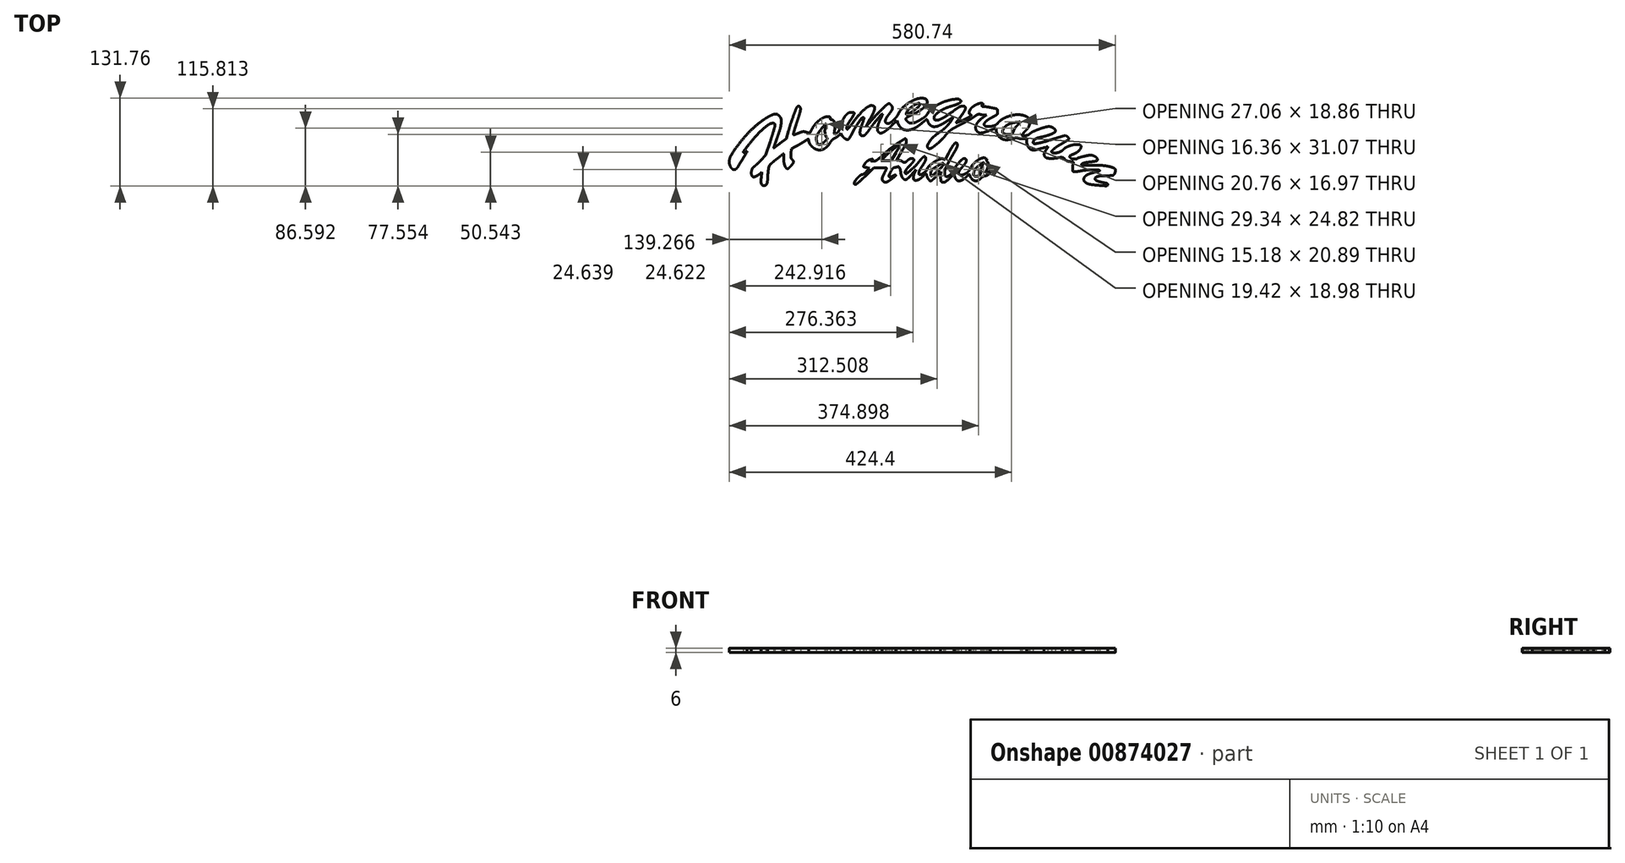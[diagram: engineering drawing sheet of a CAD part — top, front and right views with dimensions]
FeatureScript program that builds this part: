
annotation { "Feature Type Name" : "Feature", "Feature Type Description" : "" }
export const myFeature = defineFeature(function(context is Context, id is Id, definition is map)
    precondition{}
    {
        {
            var Q0;
            Q0=qCreatedBy(makeId("Top.planeOp"),FACE);
            var sketch = newSketch(context, id + "F0", { "sketchPlane" : qUnion([Q0])});
            skArc(sketch, "E0", {"start": v(-9.14, 64.5) * mm, "mid": v(-13.46, 62.75) * mm, "end": v(-17.6, 60.6) * mm});
            skArc(sketch, "E1", {"start": v(-17.6, 60.6) * mm, "mid": v(-21.63, 58.07) * mm, "end": v(-25.43, 55.2) * mm});
            skArc(sketch, "E2", {"start": v(-25.43, 55.2) * mm, "mid": v(-28.76, 52.2) * mm, "end": v(-31.81, 48.92) * mm});
            skArc(sketch, "E3", {"start": v(-31.81, 48.92) * mm, "mid": v(-34.1, 45.82) * mm, "end": v(-35.94, 42.44) * mm});
            skArc(sketch, "E4", {"start": v(-35.94, 42.44) * mm, "mid": v(-36.95, 40.52) * mm, "end": v(-38.16, 38.74) * mm});
            skArc(sketch, "E5", {"start": v(-38.16, 38.74) * mm, "mid": v(-39.88, 36.6) * mm, "end": v(-41.73, 34.56) * mm});
            skArc(sketch, "E6", {"start": v(-41.73, 34.56) * mm, "mid": v(-43.68, 32.62) * mm, "end": v(-45.74, 30.8) * mm});
            skArc(sketch, "E7", {"start": v(-45.74, 30.8) * mm, "mid": v(-47.5, 29.48) * mm, "end": v(-49.38, 28.36) * mm});
            skArc(sketch, "E8", {"start": v(-49.38, 28.36) * mm, "mid": v(-50.4, 27.96) * mm, "end": v(-51.5, 27.79) * mm});
            skArc(sketch, "E9", {"start": v(-51.5, 27.79) * mm, "mid": v(-52.56, 27.87) * mm, "end": v(-53.58, 28.21) * mm});
            skArc(sketch, "E10", {"start": v(-53.58, 28.21) * mm, "mid": v(-54.41, 28.76) * mm, "end": v(-55.07, 29.51) * mm});
            skArc(sketch, "E11", {"start": v(-55.07, 29.51) * mm, "mid": v(-55.48, 30.4) * mm, "end": v(-55.63, 31.35) * mm});
            skArc(sketch, "E12", {"start": v(-55.63, 31.35) * mm, "mid": v(-55.54, 32.43) * mm, "end": v(-55.28, 33.49) * mm});
            skArc(sketch, "E13", {"start": v(-55.28, 33.49) * mm, "mid": v(-54.82, 34.7) * mm, "end": v(-54.25, 35.85) * mm});
            skArc(sketch, "E14", {"start": v(-54.25, 35.85) * mm, "mid": v(-53.33, 37.4) * mm, "end": v(-52.32, 38.88) * mm});
            skArc(sketch, "E15", {"start": v(-52.32, 38.88) * mm, "mid": v(-50.67, 41.1) * mm, "end": v(-48.97, 43.31) * mm});
            skArc(sketch, "E16", {"start": v(-48.97, 43.31) * mm, "mid": v(-47.41, 45.42) * mm, "end": v(-45.95, 47.6) * mm});
            skArc(sketch, "E17", {"start": v(-45.95, 47.6) * mm, "mid": v(-45.26, 48.98) * mm, "end": v(-44.87, 50.47) * mm});
            skArc(sketch, "E18", {"start": v(-44.87, 50.47) * mm, "mid": v(-44.87, 51.74) * mm, "end": v(-45.26, 52.95) * mm});
            skArc(sketch, "E19", {"start": v(-45.26, 52.95) * mm, "mid": v(-46.09, 54.36) * mm, "end": v(-47.12, 55.65) * mm});
            skArc(sketch, "E20", {"start": v(-47.12, 55.65) * mm, "mid": v(-47.8, 56.35) * mm, "end": v(-48.5, 57.01) * mm});
            skArc(sketch, "E21", {"start": v(-48.5, 57.01) * mm, "mid": v(-48.98, 57.36) * mm, "end": v(-49.5, 57.61) * mm});
            skArc(sketch, "E22", {"start": v(-49.5, 57.61) * mm, "mid": v(-49.98, 57.71) * mm, "end": v(-50.45, 57.68) * mm});
            skArc(sketch, "E23", {"start": v(-50.45, 57.68) * mm, "mid": v(-51.03, 57.52) * mm, "end": v(-51.58, 57.28) * mm});
            skArc(sketch, "E24", {"start": v(-51.58, 57.28) * mm, "mid": v(-53.01, 56.38) * mm, "end": v(-54.32, 55.31) * mm});
            skArc(sketch, "E25", {"start": v(-54.32, 55.31) * mm, "mid": v(-57.3, 52.5) * mm, "end": v(-60.23, 49.63) * mm});
            skArc(sketch, "E26", {"start": v(-60.23, 49.63) * mm, "mid": v(-63.84, 46.03) * mm, "end": v(-67.38, 42.37) * mm});
            skArc(sketch, "E27", {"start": v(-67.38, 42.37) * mm, "mid": v(-71.44, 38.08) * mm, "end": v(-75.46, 33.75) * mm});
            skLineSegment(sketch, "E28", {"start": v(-75.46, 33.75) * mm, "end": v(-84.65, 23.75) * mm});
            skLineSegment(sketch, "E29", {"start": v(-84.65, 23.75) * mm, "end": v(-78.56, 34.4) * mm});
            skArc(sketch, "E30", {"start": v(-78.56, 34.4) * mm, "mid": v(-77.3, 36.66) * mm, "end": v(-76.1, 38.93) * mm});
            skArc(sketch, "E31", {"start": v(-76.1, 38.93) * mm, "mid": v(-75.03, 41.05) * mm, "end": v(-74.03, 43.2) * mm});
            skArc(sketch, "E32", {"start": v(-74.03, 43.2) * mm, "mid": v(-73.24, 45.02) * mm, "end": v(-72.5, 46.85) * mm});
            skArc(sketch, "E33", {"start": v(-72.5, 46.85) * mm, "mid": v(-72.14, 47.97) * mm, "end": v(-71.92, 49.12) * mm});
            skArc(sketch, "E34", {"start": v(-71.92, 49.12) * mm, "mid": v(-71.78, 50.3) * mm, "end": v(-71.69, 51.49) * mm});
            skArc(sketch, "E35", {"start": v(-71.69, 51.49) * mm, "mid": v(-71.72, 52.11) * mm, "end": v(-71.89, 52.71) * mm});
            skArc(sketch, "E36", {"start": v(-71.89, 52.71) * mm, "mid": v(-72.16, 53.18) * mm, "end": v(-72.55, 53.56) * mm});
            skArc(sketch, "E37", {"start": v(-72.55, 53.56) * mm, "mid": v(-73.25, 54) * mm, "end": v(-73.99, 54.37) * mm});
            skArc(sketch, "E38", {"start": v(-73.99, 54.37) * mm, "mid": v(-76.57, 54.92) * mm, "end": v(-79.15, 54.34) * mm});
            skArc(sketch, "E39", {"start": v(-79.15, 54.34) * mm, "mid": v(-82.75, 52.35) * mm, "end": v(-86.06, 49.93) * mm});
            skArc(sketch, "E40", {"start": v(-86.06, 49.93) * mm, "mid": v(-90.45, 45.95) * mm, "end": v(-94.48, 41.6) * mm});
            skArc(sketch, "E41", {"start": v(-94.48, 41.6) * mm, "mid": v(-99.58, 35.4) * mm, "end": v(-104.46, 29) * mm});
            skArc(sketch, "E42", {"start": v(-104.46, 29) * mm, "mid": v(-105.86, 27.12) * mm, "end": v(-107.29, 25.26) * mm});
            skArc(sketch, "E43", {"start": v(-107.29, 25.26) * mm, "mid": v(-108.54, 23.68) * mm, "end": v(-109.82, 22.12) * mm});
            skArc(sketch, "E44", {"start": v(-109.82, 22.12) * mm, "mid": v(-110.92, 20.82) * mm, "end": v(-112.03, 19.52) * mm});
            skArc(sketch, "E45", {"start": v(-112.03, 19.52) * mm, "mid": v(-112.3, 19.32) * mm, "end": v(-112.63, 19.25) * mm});
            skArc(sketch, "E46", {"start": v(-112.63, 19.25) * mm, "mid": v(-113.15, 19.43) * mm, "end": v(-113.45, 19.9) * mm});
            skArc(sketch, "E47", {"start": v(-113.45, 19.9) * mm, "mid": v(-113.58, 20.84) * mm, "end": v(-113.56, 21.78) * mm});
            skArc(sketch, "E48", {"start": v(-113.56, 21.78) * mm, "mid": v(-113.36, 23.07) * mm, "end": v(-113.01, 24.33) * mm});
            skArc(sketch, "E49", {"start": v(-113.01, 24.33) * mm, "mid": v(-112.5, 25.64) * mm, "end": v(-111.87, 26.9) * mm});
            skArc(sketch, "E50", {"start": v(-111.87, 26.9) * mm, "mid": v(-111.42, 27.69) * mm, "end": v(-110.95, 28.47) * mm});
            skArc(sketch, "E51", {"start": v(-110.95, 28.47) * mm, "mid": v(-110.26, 29.58) * mm, "end": v(-109.56, 30.7) * mm});
            skArc(sketch, "E52", {"start": v(-109.56, 30.7) * mm, "mid": v(-108.77, 31.9) * mm, "end": v(-107.98, 33.12) * mm});
            skArc(sketch, "E53", {"start": v(-107.98, 33.12) * mm, "mid": v(-107.22, 34.26) * mm, "end": v(-106.44, 35.4) * mm});
            skArc(sketch, "E54", {"start": v(-106.44, 35.4) * mm, "mid": v(-105.71, 36.49) * mm, "end": v(-105.01, 37.6) * mm});
            skArc(sketch, "E55", {"start": v(-105.01, 37.6) * mm, "mid": v(-104.37, 38.67) * mm, "end": v(-103.75, 39.77) * mm});
            skArc(sketch, "E56", {"start": v(-103.75, 39.77) * mm, "mid": v(-103.26, 40.7) * mm, "end": v(-102.78, 41.66) * mm});
            skArc(sketch, "E57", {"start": v(-102.78, 41.66) * mm, "mid": v(-102.58, 42.2) * mm, "end": v(-102.44, 42.75) * mm});
            skArc(sketch, "E58", {"start": v(-102.44, 42.75) * mm, "mid": v(-102.4, 43.28) * mm, "end": v(-102.47, 43.8) * mm});
            skArc(sketch, "E59", {"start": v(-102.47, 43.8) * mm, "mid": v(-102.62, 44.15) * mm, "end": v(-102.92, 44.4) * mm});
            skArc(sketch, "E60", {"start": v(-102.92, 44.4) * mm, "mid": v(-103.43, 44.58) * mm, "end": v(-103.98, 44.65) * mm});
            skArc(sketch, "E61", {"start": v(-103.98, 44.65) * mm, "mid": v(-105.2, 44.67) * mm, "end": v(-106.4, 44.66) * mm});
            skArc(sketch, "E62", {"start": v(-106.4, 44.66) * mm, "mid": v(-107.52, 44.6) * mm, "end": v(-108.64, 44.47) * mm});
            skArc(sketch, "E63", {"start": v(-108.64, 44.47) * mm, "mid": v(-109.54, 44.28) * mm, "end": v(-110.4, 43.98) * mm});
            skArc(sketch, "E64", {"start": v(-110.4, 43.98) * mm, "mid": v(-111.23, 43.59) * mm, "end": v(-112, 43.1) * mm});
            skArc(sketch, "E65", {"start": v(-112, 43.1) * mm, "mid": v(-112.87, 42.43) * mm, "end": v(-113.68, 41.7) * mm});
            skArc(sketch, "E66", {"start": v(-113.68, 41.7) * mm, "mid": v(-115.24, 40.02) * mm, "end": v(-116.6, 38.16) * mm});
            skArc(sketch, "E67", {"start": v(-116.6, 38.16) * mm, "mid": v(-118.15, 35.6) * mm, "end": v(-119.56, 32.96) * mm});
            skArc(sketch, "E68", {"start": v(-119.56, 32.96) * mm, "mid": v(-120.84, 30.2) * mm, "end": v(-121.98, 27.39) * mm});
            skArc(sketch, "E69", {"start": v(-121.98, 27.39) * mm, "mid": v(-122.7, 25.07) * mm, "end": v(-123.19, 22.68) * mm});
            skArc(sketch, "E70", {"start": v(-123.19, 22.68) * mm, "mid": v(-123.6, 20.86) * mm, "end": v(-124.25, 19.12) * mm});
            skArc(sketch, "E71", {"start": v(-124.25, 19.12) * mm, "mid": v(-125.19, 17.33) * mm, "end": v(-126.32, 15.66) * mm});
            skArc(sketch, "E72", {"start": v(-126.32, 15.66) * mm, "mid": v(-127.49, 14.3) * mm, "end": v(-128.81, 13.07) * mm});
            skArc(sketch, "E73", {"start": v(-128.81, 13.07) * mm, "mid": v(-129.89, 12.46) * mm, "end": v(-131.1, 12.25) * mm});
            skArc(sketch, "E74", {"start": v(-131.1, 12.25) * mm, "mid": v(-131.5, 12.29) * mm, "end": v(-131.89, 12.4) * mm});
            skArc(sketch, "E75", {"start": v(-131.89, 12.4) * mm, "mid": v(-132.14, 12.57) * mm, "end": v(-132.32, 12.83) * mm});
            skArc(sketch, "E76", {"start": v(-132.32, 12.83) * mm, "mid": v(-132.43, 13.22) * mm, "end": v(-132.44, 13.63) * mm});
            skArc(sketch, "E77", {"start": v(-132.44, 13.63) * mm, "mid": v(-132.36, 14.32) * mm, "end": v(-132.24, 15) * mm});
            skArc(sketch, "E78", {"start": v(-132.24, 15) * mm, "mid": v(-132.13, 15.63) * mm, "end": v(-132.03, 16.27) * mm});
            skArc(sketch, "E79", {"start": v(-132.03, 16.27) * mm, "mid": v(-131.92, 17.05) * mm, "end": v(-131.82, 17.83) * mm});
            skArc(sketch, "E80", {"start": v(-131.82, 17.83) * mm, "mid": v(-131.73, 18.61) * mm, "end": v(-131.65, 19.4) * mm});
            skArc(sketch, "E81", {"start": v(-131.65, 19.4) * mm, "mid": v(-131.6, 20.08) * mm, "end": v(-131.56, 20.75) * mm});
            skArc(sketch, "E82", {"start": v(-131.56, 20.75) * mm, "mid": v(-131.48, 23.72) * mm, "end": v(-131.54, 26.7) * mm});
            skArc(sketch, "E83", {"start": v(-131.54, 26.7) * mm, "mid": v(-131.78, 28.6) * mm, "end": v(-132.3, 30.43) * mm});
            skArc(sketch, "E84", {"start": v(-132.3, 30.43) * mm, "mid": v(-132.96, 31.61) * mm, "end": v(-133.91, 32.57) * mm});
            skArc(sketch, "E85", {"start": v(-133.91, 32.57) * mm, "mid": v(-135.08, 33.22) * mm, "end": v(-136.4, 33.5) * mm});
            skArc(sketch, "E86", {"start": v(-136.4, 33.5) * mm, "mid": v(-136.82, 33.56) * mm, "end": v(-137.23, 33.65) * mm});
            skArc(sketch, "E87", {"start": v(-137.23, 33.65) * mm, "mid": v(-137.6, 33.77) * mm, "end": v(-137.93, 33.93) * mm});
            skArc(sketch, "E88", {"start": v(-137.93, 33.93) * mm, "mid": v(-138.17, 34.1) * mm, "end": v(-138.38, 34.3) * mm});
            skArc(sketch, "E89", {"start": v(-138.38, 34.3) * mm, "mid": v(-138.48, 34.5) * mm, "end": v(-138.5, 34.71) * mm});
            skArc(sketch, "E90", {"start": v(-138.5, 34.71) * mm, "mid": v(-138.45, 35.62) * mm, "end": v(-138.48, 36.52) * mm});
            skArc(sketch, "E91", {"start": v(-138.48, 36.52) * mm, "mid": v(-138.62, 37.07) * mm, "end": v(-138.94, 37.55) * mm});
            skArc(sketch, "E92", {"start": v(-138.94, 37.55) * mm, "mid": v(-139.4, 37.9) * mm, "end": v(-139.96, 38.09) * mm});
            skArc(sketch, "E93", {"start": v(-139.96, 38.09) * mm, "mid": v(-140.92, 38.2) * mm, "end": v(-141.88, 38.23) * mm});
            skArc(sketch, "E94", {"start": v(-141.88, 38.23) * mm, "mid": v(-145.08, 37.85) * mm, "end": v(-148.13, 36.79) * mm});
            skArc(sketch, "E95", {"start": v(-148.13, 36.79) * mm, "mid": v(-151.72, 34.83) * mm, "end": v(-155.06, 32.48) * mm});
            skArc(sketch, "E96", {"start": v(-155.06, 32.48) * mm, "mid": v(-158.42, 29.55) * mm, "end": v(-161.46, 26.29) * mm});
            skArc(sketch, "E97", {"start": v(-161.46, 26.29) * mm, "mid": v(-164.02, 22.85) * mm, "end": v(-166.16, 19.13) * mm});
            skArc(sketch, "E98", {"start": v(-166.16, 19.13) * mm, "mid": v(-166.69, 18.09) * mm, "end": v(-167.22, 17.05) * mm});
            skArc(sketch, "E99", {"start": v(-167.22, 17.05) * mm, "mid": v(-167.69, 16.14) * mm, "end": v(-168.16, 15.24) * mm});
            skArc(sketch, "E100", {"start": v(-168.16, 15.24) * mm, "mid": v(-168.56, 14.46) * mm, "end": v(-168.97, 13.7) * mm});
            skArc(sketch, "E101", {"start": v(-168.97, 13.7) * mm, "mid": v(-169.05, 13.55) * mm, "end": v(-169.15, 13.43) * mm});
            skArc(sketch, "E102", {"start": v(-169.15, 13.43) * mm, "mid": v(-169.27, 13.35) * mm, "end": v(-169.4, 13.35) * mm});
            skArc(sketch, "E103", {"start": v(-169.4, 13.35) * mm, "mid": v(-170.05, 13.5) * mm, "end": v(-170.7, 13.66) * mm});
            skArc(sketch, "E104", {"start": v(-170.7, 13.66) * mm, "mid": v(-171.48, 13.87) * mm, "end": v(-172.25, 14.1) * mm});
            skArc(sketch, "E105", {"start": v(-172.25, 14.1) * mm, "mid": v(-173.14, 14.37) * mm, "end": v(-174.02, 14.67) * mm});
            skArc(sketch, "E106", {"start": v(-174.02, 14.67) * mm, "mid": v(-175.46, 15.12) * mm, "end": v(-176.92, 15.5) * mm});
            skArc(sketch, "E107", {"start": v(-176.92, 15.5) * mm, "mid": v(-177.88, 15.66) * mm, "end": v(-178.85, 15.67) * mm});
            skArc(sketch, "E108", {"start": v(-178.85, 15.67) * mm, "mid": v(-179.92, 15.53) * mm, "end": v(-180.96, 15.25) * mm});
            skArc(sketch, "E109", {"start": v(-180.96, 15.25) * mm, "mid": v(-182.92, 14.59) * mm, "end": v(-184.87, 13.88) * mm});
            skArc(sketch, "E110", {"start": v(-184.87, 13.88) * mm, "mid": v(-186.13, 13.4) * mm, "end": v(-187.4, 12.93) * mm});
            skArc(sketch, "E111", {"start": v(-187.4, 12.93) * mm, "mid": v(-188.6, 12.47) * mm, "end": v(-189.8, 12) * mm});
            skArc(sketch, "E112", {"start": v(-189.8, 12) * mm, "mid": v(-190.8, 11.61) * mm, "end": v(-191.82, 11.22) * mm});
            skArc(sketch, "E113", {"start": v(-191.82, 11.22) * mm, "mid": v(-192.33, 11.01) * mm, "end": v(-192.84, 10.8) * mm});
            skArc(sketch, "E114", {"start": v(-192.84, 10.8) * mm, "mid": v(-193.23, 10.7) * mm, "end": v(-193.64, 10.75) * mm});
            skArc(sketch, "E115", {"start": v(-193.64, 10.75) * mm, "mid": v(-193.9, 10.93) * mm, "end": v(-194, 11.23) * mm});
            skArc(sketch, "E116", {"start": v(-194, 11.23) * mm, "mid": v(-193.92, 11.98) * mm, "end": v(-193.77, 12.71) * mm});
            skArc(sketch, "E117", {"start": v(-193.77, 12.71) * mm, "mid": v(-193.2, 14.81) * mm, "end": v(-192.63, 16.9) * mm});
            skArc(sketch, "E118", {"start": v(-192.63, 16.9) * mm, "mid": v(-192.13, 18.63) * mm, "end": v(-191.62, 20.35) * mm});
            skArc(sketch, "E119", {"start": v(-191.62, 20.35) * mm, "mid": v(-190.85, 22.81) * mm, "end": v(-190.08, 25.27) * mm});
            skArc(sketch, "E120", {"start": v(-190.08, 25.27) * mm, "mid": v(-189.22, 27.96) * mm, "end": v(-188.34, 30.66) * mm});
            skArc(sketch, "E121", {"start": v(-188.34, 30.66) * mm, "mid": v(-187.5, 33.2) * mm, "end": v(-186.65, 35.75) * mm});
            skArc(sketch, "E122", {"start": v(-186.65, 35.75) * mm, "mid": v(-185.73, 38.53) * mm, "end": v(-184.85, 41.32) * mm});
            skArc(sketch, "E123", {"start": v(-184.85, 41.32) * mm, "mid": v(-184.25, 43.41) * mm, "end": v(-183.72, 45.52) * mm});
            skArc(sketch, "E124", {"start": v(-183.72, 45.52) * mm, "mid": v(-183.4, 47.08) * mm, "end": v(-183.13, 48.66) * mm});
            skArc(sketch, "E125", {"start": v(-183.13, 48.66) * mm, "mid": v(-183.08, 49.62) * mm, "end": v(-183.2, 50.57) * mm});
            skArc(sketch, "E126", {"start": v(-183.2, 50.57) * mm, "mid": v(-183.53, 51.66) * mm, "end": v(-184.02, 52.69) * mm});
            skArc(sketch, "E127", {"start": v(-184.02, 52.69) * mm, "mid": v(-184.58, 53.39) * mm, "end": v(-185.33, 53.88) * mm});
            skArc(sketch, "E128", {"start": v(-185.33, 53.88) * mm, "mid": v(-186.07, 54.06) * mm, "end": v(-186.81, 53.92) * mm});
            skArc(sketch, "E129", {"start": v(-186.81, 53.92) * mm, "mid": v(-187.57, 53.48) * mm, "end": v(-188.17, 52.86) * mm});
            skArc(sketch, "E130", {"start": v(-188.17, 52.86) * mm, "mid": v(-189.3, 51.09) * mm, "end": v(-190.17, 49.18) * mm});
            skArc(sketch, "E131", {"start": v(-190.17, 49.18) * mm, "mid": v(-192.16, 43.86) * mm, "end": v(-194.1, 38.5) * mm});
            skArc(sketch, "E132", {"start": v(-194.1, 38.5) * mm, "mid": v(-196.12, 32.75) * mm, "end": v(-198.04, 26.96) * mm});
            skArc(sketch, "E133", {"start": v(-198.04, 26.96) * mm, "mid": v(-199.63, 21.87) * mm, "end": v(-201.1, 16.75) * mm});
            skLineSegment(sketch, "E134", {"start": v(-201.1, 16.75) * mm, "end": v(-204.38, 4.75) * mm});
            skLineSegment(sketch, "E135", {"start": v(-204.38, 4.75) * mm, "end": v(-213.75, -2) * mm});
            skArc(sketch, "E136", {"start": v(-213.75, -2) * mm, "mid": v(-215.56, -3.3) * mm, "end": v(-217.36, -4.58) * mm});
            skArc(sketch, "E137", {"start": v(-217.36, -4.58) * mm, "mid": v(-218.9, -5.67) * mm, "end": v(-220.43, -6.76) * mm});
            skArc(sketch, "E138", {"start": v(-220.43, -6.76) * mm, "mid": v(-221.8, -7.73) * mm, "end": v(-223.18, -8.7) * mm});
            skArc(sketch, "E139", {"start": v(-223.18, -8.7) * mm, "mid": v(-223.25, -8.73) * mm, "end": v(-223.33, -8.75) * mm});
            skArc(sketch, "E140", {"start": v(-223.33, -8.75) * mm, "mid": v(-223.38, -8.72) * mm, "end": v(-223.4, -8.67) * mm});
            skArc(sketch, "E141", {"start": v(-223.4, -8.67) * mm, "mid": v(-222.62, -6.4) * mm, "end": v(-221.84, -4.12) * mm});
            skArc(sketch, "E142", {"start": v(-221.84, -4.12) * mm, "mid": v(-220.97, -1.58) * mm, "end": v(-220.09, 0.96) * mm});
            skArc(sketch, "E143", {"start": v(-220.09, 0.96) * mm, "mid": v(-219.03, 3.98) * mm, "end": v(-217.96, 7) * mm});
            skArc(sketch, "E144", {"start": v(-217.96, 7) * mm, "mid": v(-216.5, 11.17) * mm, "end": v(-215.1, 15.36) * mm});
            skArc(sketch, "E145", {"start": v(-215.1, 15.36) * mm, "mid": v(-214.23, 18.14) * mm, "end": v(-213.47, 20.94) * mm});
            skArc(sketch, "E146", {"start": v(-213.47, 20.94) * mm, "mid": v(-212.97, 23.11) * mm, "end": v(-212.6, 25.3) * mm});
            skArc(sketch, "E147", {"start": v(-212.6, 25.3) * mm, "mid": v(-212.36, 27.36) * mm, "end": v(-212.25, 29.43) * mm});
            skArc(sketch, "E148", {"start": v(-212.25, 29.43) * mm, "mid": v(-212.24, 31.42) * mm, "end": v(-212.27, 33.41) * mm});
            skArc(sketch, "E149", {"start": v(-212.27, 33.41) * mm, "mid": v(-212.37, 34.5) * mm, "end": v(-212.61, 35.56) * mm});
            skArc(sketch, "E150", {"start": v(-212.61, 35.56) * mm, "mid": v(-212.95, 36.44) * mm, "end": v(-213.44, 37.24) * mm});
            skArc(sketch, "E151", {"start": v(-213.44, 37.24) * mm, "mid": v(-214.25, 38.28) * mm, "end": v(-215.13, 39.27) * mm});
            skArc(sketch, "E152", {"start": v(-215.13, 39.27) * mm, "mid": v(-216, 40.14) * mm, "end": v(-216.9, 40.96) * mm});
            skArc(sketch, "E153", {"start": v(-216.9, 40.96) * mm, "mid": v(-217.55, 41.43) * mm, "end": v(-218.26, 41.79) * mm});
            skArc(sketch, "E154", {"start": v(-218.26, 41.79) * mm, "mid": v(-219, 42) * mm, "end": v(-219.75, 42.07) * mm});
            skArc(sketch, "E155", {"start": v(-219.75, 42.07) * mm, "mid": v(-220.84, 42.03) * mm, "end": v(-221.92, 41.93) * mm});
            skArc(sketch, "E156", {"start": v(-221.92, 41.93) * mm, "mid": v(-224.12, 41.46) * mm, "end": v(-226.22, 40.65) * mm});
            skArc(sketch, "E157", {"start": v(-226.22, 40.65) * mm, "mid": v(-229.42, 39.04) * mm, "end": v(-232.54, 37.3) * mm});
            skArc(sketch, "E158", {"start": v(-232.54, 37.3) * mm, "mid": v(-236.17, 35.07) * mm, "end": v(-239.7, 32.7) * mm});
            skArc(sketch, "E159", {"start": v(-239.7, 32.7) * mm, "mid": v(-243.39, 30.03) * mm, "end": v(-246.98, 27.24) * mm});
            skArc(sketch, "E160", {"start": v(-246.98, 27.24) * mm, "mid": v(-254.3, 20.93) * mm, "end": v(-261.18, 14.13) * mm});
            skArc(sketch, "E161", {"start": v(-261.18, 14.13) * mm, "mid": v(-268.42, 6.1) * mm, "end": v(-275.26, -2.27) * mm});
            skArc(sketch, "E162", {"start": v(-275.26, -2.27) * mm, "mid": v(-281.1, -10.15) * mm, "end": v(-286.58, -18.28) * mm});
            skArc(sketch, "E163", {"start": v(-286.58, -18.28) * mm, "mid": v(-289, -23.19) * mm, "end": v(-290.29, -28.52) * mm});
            skArc(sketch, "E164", {"start": v(-290.29, -28.52) * mm, "mid": v(-290.36, -30.54) * mm, "end": v(-290.07, -32.55) * mm});
            skArc(sketch, "E165", {"start": v(-290.07, -32.55) * mm, "mid": v(-289.42, -34.74) * mm, "end": v(-288.5, -36.83) * mm});
            skArc(sketch, "E166", {"start": v(-288.5, -36.83) * mm, "mid": v(-287.43, -38.6) * mm, "end": v(-286.14, -40.23) * mm});
            skArc(sketch, "E167", {"start": v(-286.14, -40.23) * mm, "mid": v(-284.97, -41.12) * mm, "end": v(-283.57, -41.55) * mm});
            skArc(sketch, "E168", {"start": v(-283.57, -41.55) * mm, "mid": v(-283, -41.58) * mm, "end": v(-282.44, -41.54) * mm});
            skArc(sketch, "E169", {"start": v(-282.44, -41.54) * mm, "mid": v(-281.85, -41.43) * mm, "end": v(-281.28, -41.26) * mm});
            skArc(sketch, "E170", {"start": v(-281.28, -41.26) * mm, "mid": v(-280.74, -41.03) * mm, "end": v(-280.23, -40.74) * mm});
            skArc(sketch, "E171", {"start": v(-280.23, -40.74) * mm, "mid": v(-279.79, -40.42) * mm, "end": v(-279.4, -40.05) * mm});
            skArc(sketch, "E172", {"start": v(-279.4, -40.05) * mm, "mid": v(-278.3, -38.72) * mm, "end": v(-277.33, -37.3) * mm});
            skArc(sketch, "E173", {"start": v(-277.33, -37.3) * mm, "mid": v(-274.07, -32.01) * mm, "end": v(-270.83, -26.7) * mm});
            skArc(sketch, "E174", {"start": v(-270.83, -26.7) * mm, "mid": v(-267.4, -21.07) * mm, "end": v(-263.98, -15.43) * mm});
            skArc(sketch, "E175", {"start": v(-263.98, -15.43) * mm, "mid": v(-263.72, -14.8) * mm, "end": v(-263.63, -14.14) * mm});
            skArc(sketch, "E176", {"start": v(-263.63, -14.14) * mm, "mid": v(-263.68, -14.04) * mm, "end": v(-263.8, -14) * mm});
            skArc(sketch, "E177", {"start": v(-263.8, -14) * mm, "mid": v(-264.1, -14.1) * mm, "end": v(-264.39, -14.2) * mm});
            skArc(sketch, "E178", {"start": v(-264.39, -14.2) * mm, "mid": v(-264.8, -14.4) * mm, "end": v(-265.22, -14.6) * mm});
            skArc(sketch, "E179", {"start": v(-265.22, -14.6) * mm, "mid": v(-265.72, -14.9) * mm, "end": v(-266.21, -15.21) * mm});
            skArc(sketch, "E180", {"start": v(-266.21, -15.21) * mm, "mid": v(-267.25, -15.7) * mm, "end": v(-268.38, -15.88) * mm});
            skArc(sketch, "E181", {"start": v(-268.38, -15.88) * mm, "mid": v(-268.93, -15.58) * mm, "end": v(-268.95, -14.95) * mm});
            skArc(sketch, "E182", {"start": v(-268.95, -14.95) * mm, "mid": v(-267.65, -12.7) * mm, "end": v(-266.15, -10.58) * mm});
            skArc(sketch, "E183", {"start": v(-266.15, -10.58) * mm, "mid": v(-262.7, -6.15) * mm, "end": v(-259.18, -1.76) * mm});
            skArc(sketch, "E184", {"start": v(-259.18, -1.76) * mm, "mid": v(-253.92, 4.55) * mm, "end": v(-248.47, 10.69) * mm});
            skArc(sketch, "E185", {"start": v(-248.47, 10.69) * mm, "mid": v(-243.75, 15.56) * mm, "end": v(-238.78, 20.17) * mm});
            skArc(sketch, "E186", {"start": v(-238.78, 20.17) * mm, "mid": v(-234.77, 23.48) * mm, "end": v(-230.57, 26.54) * mm});
            skArc(sketch, "E187", {"start": v(-230.57, 26.54) * mm, "mid": v(-227.93, 27.81) * mm, "end": v(-225.03, 28.25) * mm});
            skArc(sketch, "E188", {"start": v(-225.03, 28.25) * mm, "mid": v(-224.01, 28.23) * mm, "end": v(-223, 28.16) * mm});
            skArc(sketch, "E189", {"start": v(-223, 28.16) * mm, "mid": v(-222.54, 28.03) * mm, "end": v(-222.14, 27.76) * mm});
            skArc(sketch, "E190", {"start": v(-222.14, 27.76) * mm, "mid": v(-221.86, 27.38) * mm, "end": v(-221.73, 26.93) * mm});
            skArc(sketch, "E191", {"start": v(-221.73, 26.93) * mm, "mid": v(-221.66, 25.97) * mm, "end": v(-221.64, 25) * mm});
            skArc(sketch, "E192", {"start": v(-221.64, 25) * mm, "mid": v(-221.72, 23.92) * mm, "end": v(-221.93, 22.86) * mm});
            skArc(sketch, "E193", {"start": v(-221.93, 22.86) * mm, "mid": v(-222.8, 19.71) * mm, "end": v(-223.69, 16.58) * mm});
            skArc(sketch, "E194", {"start": v(-223.69, 16.58) * mm, "mid": v(-224.79, 12.84) * mm, "end": v(-225.93, 9.12) * mm});
            skArc(sketch, "E195", {"start": v(-225.93, 9.12) * mm, "mid": v(-227.24, 5) * mm, "end": v(-228.59, 0.89) * mm});
            skLineSegment(sketch, "E196", {"start": v(-228.59, 0.89) * mm, "end": v(-235.5, -19.98) * mm});
            skLineSegment(sketch, "E197", {"start": v(-235.5, -19.98) * mm, "end": v(-242.82, -27.61) * mm});
            skArc(sketch, "E198", {"start": v(-242.82, -27.61) * mm, "mid": v(-244.3, -29.15) * mm, "end": v(-245.81, -30.66) * mm});
            skArc(sketch, "E199", {"start": v(-245.81, -30.66) * mm, "mid": v(-247.28, -32.1) * mm, "end": v(-248.77, -33.5) * mm});
            skArc(sketch, "E200", {"start": v(-248.77, -33.5) * mm, "mid": v(-250.05, -34.68) * mm, "end": v(-251.35, -35.85) * mm});
            skArc(sketch, "E201", {"start": v(-251.35, -35.85) * mm, "mid": v(-252.07, -36.43) * mm, "end": v(-252.82, -36.95) * mm});
            skArc(sketch, "E202", {"start": v(-252.82, -36.95) * mm, "mid": v(-254.48, -38.36) * mm, "end": v(-255.67, -40.19) * mm});
            skArc(sketch, "E203", {"start": v(-255.67, -40.19) * mm, "mid": v(-256.55, -42.62) * mm, "end": v(-257, -45.16) * mm});
            skArc(sketch, "E204", {"start": v(-257, -45.16) * mm, "mid": v(-257, -47.53) * mm, "end": v(-256.54, -49.86) * mm});
            skArc(sketch, "E205", {"start": v(-256.54, -49.86) * mm, "mid": v(-255.67, -51.37) * mm, "end": v(-254.23, -52.35) * mm});
            skArc(sketch, "E206", {"start": v(-254.23, -52.35) * mm, "mid": v(-253.38, -52.52) * mm, "end": v(-252.53, -52.4) * mm});
            skArc(sketch, "E207", {"start": v(-252.53, -52.4) * mm, "mid": v(-251.05, -51.86) * mm, "end": v(-249.62, -51.24) * mm});
            skArc(sketch, "E208", {"start": v(-249.62, -51.24) * mm, "mid": v(-248.02, -50.41) * mm, "end": v(-246.49, -49.48) * mm});
            skArc(sketch, "E209", {"start": v(-246.49, -49.48) * mm, "mid": v(-245.1, -48.48) * mm, "end": v(-243.79, -47.38) * mm});
            skLineSegment(sketch, "E210", {"start": v(-243.79, -47.38) * mm, "end": v(-241.45, -45.25) * mm});
            skLineSegment(sketch, "E211", {"start": v(-241.45, -45.25) * mm, "end": v(-242.15, -53.35) * mm});
            skArc(sketch, "E212", {"start": v(-242.15, -53.35) * mm, "mid": v(-242.36, -56.36) * mm, "end": v(-242.44, -59.39) * mm});
            skArc(sketch, "E213", {"start": v(-242.44, -59.39) * mm, "mid": v(-242.3, -61.23) * mm, "end": v(-241.88, -63.02) * mm});
            skArc(sketch, "E214", {"start": v(-241.88, -63.02) * mm, "mid": v(-241.32, -64.12) * mm, "end": v(-240.45, -65) * mm});
            skArc(sketch, "E215", {"start": v(-240.45, -65) * mm, "mid": v(-239.36, -65.56) * mm, "end": v(-238.15, -65.75) * mm});
            skArc(sketch, "E216", {"start": v(-238.15, -65.75) * mm, "mid": v(-236.95, -65.58) * mm, "end": v(-235.84, -65.07) * mm});
            skArc(sketch, "E217", {"start": v(-235.84, -65.07) * mm, "mid": v(-234.85, -64.25) * mm, "end": v(-234.08, -63.2) * mm});
            skArc(sketch, "E218", {"start": v(-234.08, -63.2) * mm, "mid": v(-233.4, -61.74) * mm, "end": v(-232.98, -60.17) * mm});
            skArc(sketch, "E219", {"start": v(-232.98, -60.17) * mm, "mid": v(-232.71, -58.14) * mm, "end": v(-232.63, -56.1) * mm});
            skArc(sketch, "E220", {"start": v(-232.63, -56.1) * mm, "mid": v(-232.6, -54.83) * mm, "end": v(-232.55, -53.56) * mm});
            skArc(sketch, "E221", {"start": v(-232.55, -53.56) * mm, "mid": v(-232.45, -51.84) * mm, "end": v(-232.32, -50.12) * mm});
            skArc(sketch, "E222", {"start": v(-232.32, -50.12) * mm, "mid": v(-232.16, -48.28) * mm, "end": v(-231.98, -46.45) * mm});
            skArc(sketch, "E223", {"start": v(-231.98, -46.45) * mm, "mid": v(-231.8, -44.76) * mm, "end": v(-231.58, -43.07) * mm});
            skArc(sketch, "E224", {"start": v(-231.58, -43.07) * mm, "mid": v(-231.27, -40.94) * mm, "end": v(-230.91, -38.8) * mm});
            skArc(sketch, "E225", {"start": v(-230.91, -38.8) * mm, "mid": v(-230.62, -37.52) * mm, "end": v(-230.22, -36.27) * mm});
            skArc(sketch, "E226", {"start": v(-230.22, -36.27) * mm, "mid": v(-229.8, -35.34) * mm, "end": v(-229.27, -34.48) * mm});
            skArc(sketch, "E227", {"start": v(-229.27, -34.48) * mm, "mid": v(-228.6, -33.65) * mm, "end": v(-227.83, -32.9) * mm});
            skArc(sketch, "E228", {"start": v(-227.83, -32.9) * mm, "mid": v(-225.43, -30.86) * mm, "end": v(-223, -28.85) * mm});
            skArc(sketch, "E229", {"start": v(-223, -28.85) * mm, "mid": v(-219.7, -26.2) * mm, "end": v(-216.4, -23.57) * mm});
            skArc(sketch, "E230", {"start": v(-216.4, -23.57) * mm, "mid": v(-212.86, -20.77) * mm, "end": v(-209.31, -17.98) * mm});
            skArc(sketch, "E231", {"start": v(-209.31, -17.98) * mm, "mid": v(-209, -17.8) * mm, "end": v(-208.65, -17.75) * mm});
            skArc(sketch, "E232", {"start": v(-208.65, -17.75) * mm, "mid": v(-208.51, -17.8) * mm, "end": v(-208.45, -17.93) * mm});
            skArc(sketch, "E233", {"start": v(-208.45, -17.93) * mm, "mid": v(-208.4, -18.53) * mm, "end": v(-208.38, -19.13) * mm});
            skArc(sketch, "E234", {"start": v(-208.38, -19.13) * mm, "mid": v(-208.37, -19.88) * mm, "end": v(-208.38, -20.64) * mm});
            skArc(sketch, "E235", {"start": v(-208.38, -20.64) * mm, "mid": v(-208.42, -21.54) * mm, "end": v(-208.48, -22.44) * mm});
            skArc(sketch, "E236", {"start": v(-208.48, -22.44) * mm, "mid": v(-208.57, -24.85) * mm, "end": v(-208.46, -27.25) * mm});
            skArc(sketch, "E237", {"start": v(-208.46, -27.25) * mm, "mid": v(-208.13, -29.82) * mm, "end": v(-207.63, -32.37) * mm});
            skArc(sketch, "E238", {"start": v(-207.63, -32.37) * mm, "mid": v(-207.02, -34.62) * mm, "end": v(-206.27, -36.82) * mm});
            skArc(sketch, "E239", {"start": v(-206.27, -36.82) * mm, "mid": v(-205.56, -38.16) * mm, "end": v(-204.57, -39.3) * mm});
            skArc(sketch, "E240", {"start": v(-204.57, -39.3) * mm, "mid": v(-203.95, -39.79) * mm, "end": v(-203.27, -40.18) * mm});
            skArc(sketch, "E241", {"start": v(-203.27, -40.18) * mm, "mid": v(-202.77, -40.3) * mm, "end": v(-202.26, -40.2) * mm});
            skArc(sketch, "E242", {"start": v(-202.26, -40.2) * mm, "mid": v(-201.6, -39.83) * mm, "end": v(-201.02, -39.35) * mm});
            skArc(sketch, "E243", {"start": v(-201.02, -39.35) * mm, "mid": v(-199.56, -37.88) * mm, "end": v(-198.11, -36.4) * mm});
            skArc(sketch, "E244", {"start": v(-198.11, -36.4) * mm, "mid": v(-196.56, -34.69) * mm, "end": v(-195.09, -32.9) * mm});
            skArc(sketch, "E245", {"start": v(-195.09, -32.9) * mm, "mid": v(-194.35, -31.71) * mm, "end": v(-193.89, -30.4) * mm});
            skArc(sketch, "E246", {"start": v(-193.89, -30.4) * mm, "mid": v(-193.82, -29.33) * mm, "end": v(-194.1, -28.3) * mm});
            skArc(sketch, "E247", {"start": v(-194.1, -28.3) * mm, "mid": v(-194.79, -27.18) * mm, "end": v(-195.67, -26.21) * mm});
            skArc(sketch, "E248", {"start": v(-195.67, -26.21) * mm, "mid": v(-196.24, -25.6) * mm, "end": v(-196.72, -24.92) * mm});
            skArc(sketch, "E249", {"start": v(-196.72, -24.92) * mm, "mid": v(-197.07, -24.2) * mm, "end": v(-197.3, -23.44) * mm});
            skArc(sketch, "E250", {"start": v(-197.3, -23.44) * mm, "mid": v(-197.45, -22.35) * mm, "end": v(-197.5, -21.25) * mm});
            skArc(sketch, "E251", {"start": v(-197.5, -21.25) * mm, "mid": v(-197.48, -19.28) * mm, "end": v(-197.42, -17.3) * mm});
            skLineSegment(sketch, "E252", {"start": v(-197.42, -17.3) * mm, "end": v(-197.13, -10.25) * mm});
            skLineSegment(sketch, "E253", {"start": v(-197.13, -10.25) * mm, "end": v(-191.13, -7.17) * mm});
            skArc(sketch, "E254", {"start": v(-191.13, -7.17) * mm, "mid": v(-189.74, -6.44) * mm, "end": v(-188.37, -5.7) * mm});
            skArc(sketch, "E255", {"start": v(-188.37, -5.7) * mm, "mid": v(-186.68, -4.74) * mm, "end": v(-185, -3.77) * mm});
            skArc(sketch, "E256", {"start": v(-185, -3.77) * mm, "mid": v(-183.3, -2.76) * mm, "end": v(-181.6, -1.74) * mm});
            skArc(sketch, "E257", {"start": v(-181.6, -1.74) * mm, "mid": v(-180.16, -0.84) * mm, "end": v(-178.72, 0.08) * mm});
            skArc(sketch, "E258", {"start": v(-178.72, 0.08) * mm, "mid": v(-177.47, 0.89) * mm, "end": v(-176.2, 1.68) * mm});
            skArc(sketch, "E259", {"start": v(-176.2, 1.68) * mm, "mid": v(-175.08, 2.36) * mm, "end": v(-173.95, 3.03) * mm});
            skArc(sketch, "E260", {"start": v(-173.95, 3.03) * mm, "mid": v(-173, 3.57) * mm, "end": v(-172.03, 4.1) * mm});
            skArc(sketch, "E261", {"start": v(-172.03, 4.1) * mm, "mid": v(-171.76, 4.22) * mm, "end": v(-171.47, 4.25) * mm});
            skArc(sketch, "E262", {"start": v(-171.47, 4.25) * mm, "mid": v(-171.29, 4.2) * mm, "end": v(-171.15, 4.08) * mm});
            skArc(sketch, "E263", {"start": v(-171.15, 4.08) * mm, "mid": v(-171, 3.83) * mm, "end": v(-170.87, 3.56) * mm});
            skArc(sketch, "E264", {"start": v(-170.87, 3.56) * mm, "mid": v(-170.76, 3.19) * mm, "end": v(-170.69, 2.8) * mm});
            skArc(sketch, "E265", {"start": v(-170.69, 2.8) * mm, "mid": v(-170.64, 2.35) * mm, "end": v(-170.63, 1.9) * mm});
            skArc(sketch, "E266", {"start": v(-170.63, 1.9) * mm, "mid": v(-170.36, -0.14) * mm, "end": v(-169.58, -2.04) * mm});
            skArc(sketch, "E267", {"start": v(-169.58, -2.04) * mm, "mid": v(-168.13, -4.25) * mm, "end": v(-166.41, -6.26) * mm});
            skArc(sketch, "E268", {"start": v(-166.41, -6.26) * mm, "mid": v(-164.36, -8.14) * mm, "end": v(-162.1, -9.77) * mm});
            skArc(sketch, "E269", {"start": v(-162.1, -9.77) * mm, "mid": v(-159.9, -10.9) * mm, "end": v(-157.55, -11.63) * mm});
            skArc(sketch, "E270", {"start": v(-157.55, -11.63) * mm, "mid": v(-154.86, -11.96) * mm, "end": v(-152.16, -11.77) * mm});
            skArc(sketch, "E271", {"start": v(-152.16, -11.77) * mm, "mid": v(-149.52, -11.08) * mm, "end": v(-147.04, -9.92) * mm});
            skArc(sketch, "E272", {"start": v(-147.04, -9.92) * mm, "mid": v(-144.52, -8.16) * mm, "end": v(-142.3, -6.02) * mm});
            skArc(sketch, "E273", {"start": v(-142.3, -6.02) * mm, "mid": v(-140.03, -3.19) * mm, "end": v(-138.03, -0.15) * mm});
            skArc(sketch, "E274", {"start": v(-138.03, -0.15) * mm, "mid": v(-137.41, 0.82) * mm, "end": v(-136.73, 1.74) * mm});
            skArc(sketch, "E275", {"start": v(-136.73, 1.74) * mm, "mid": v(-136, 2.59) * mm, "end": v(-135.2, 3.38) * mm});
            skArc(sketch, "E276", {"start": v(-135.2, 3.38) * mm, "mid": v(-134.35, 4.09) * mm, "end": v(-133.46, 4.73) * mm});
            skArc(sketch, "E277", {"start": v(-133.46, 4.73) * mm, "mid": v(-132.53, 5.3) * mm, "end": v(-131.55, 5.78) * mm});
            skArc(sketch, "E278", {"start": v(-131.55, 5.78) * mm, "mid": v(-130.68, 6.21) * mm, "end": v(-129.83, 6.69) * mm});
            skArc(sketch, "E279", {"start": v(-129.83, 6.69) * mm, "mid": v(-128.9, 7.28) * mm, "end": v(-128, 7.9) * mm});
            skArc(sketch, "E280", {"start": v(-128, 7.9) * mm, "mid": v(-127.15, 8.54) * mm, "end": v(-126.33, 9.21) * mm});
            skArc(sketch, "E281", {"start": v(-126.33, 9.21) * mm, "mid": v(-125.71, 9.8) * mm, "end": v(-125.14, 10.42) * mm});
            skLineSegment(sketch, "E282", {"start": v(-125.14, 10.42) * mm, "end": v(-122.77, 13.23) * mm});
            skLineSegment(sketch, "E283", {"start": v(-122.77, 13.23) * mm, "end": v(-120.6, 9.72) * mm});
            skArc(sketch, "E284", {"start": v(-120.6, 9.72) * mm, "mid": v(-119.65, 8.35) * mm, "end": v(-118.54, 7.1) * mm});
            skArc(sketch, "E285", {"start": v(-118.54, 7.1) * mm, "mid": v(-117.29, 5.98) * mm, "end": v(-115.92, 5) * mm});
            skArc(sketch, "E286", {"start": v(-115.92, 5) * mm, "mid": v(-114.65, 4.3) * mm, "end": v(-113.3, 3.77) * mm});
            skArc(sketch, "E287", {"start": v(-113.3, 3.77) * mm, "mid": v(-112.3, 3.63) * mm, "end": v(-111.3, 3.83) * mm});
            skArc(sketch, "E288", {"start": v(-111.3, 3.83) * mm, "mid": v(-110.88, 4.06) * mm, "end": v(-110.54, 4.4) * mm});
            skArc(sketch, "E289", {"start": v(-110.54, 4.4) * mm, "mid": v(-109.86, 5.4) * mm, "end": v(-109.2, 6.41) * mm});
            skArc(sketch, "E290", {"start": v(-109.2, 6.41) * mm, "mid": v(-108.44, 7.67) * mm, "end": v(-107.72, 8.95) * mm});
            skArc(sketch, "E291", {"start": v(-107.72, 8.95) * mm, "mid": v(-106.97, 10.39) * mm, "end": v(-106.24, 11.84) * mm});
            skArc(sketch, "E292", {"start": v(-106.24, 11.84) * mm, "mid": v(-105.4, 13.54) * mm, "end": v(-104.52, 15.22) * mm});
            skArc(sketch, "E293", {"start": v(-104.52, 15.22) * mm, "mid": v(-103.4, 17.24) * mm, "end": v(-102.27, 19.23) * mm});
            skArc(sketch, "E294", {"start": v(-102.27, 19.23) * mm, "mid": v(-101.1, 21.24) * mm, "end": v(-99.9, 23.22) * mm});
            skArc(sketch, "E295", {"start": v(-99.9, 23.22) * mm, "mid": v(-98.85, 24.89) * mm, "end": v(-97.76, 26.53) * mm});
            skArc(sketch, "E296", {"start": v(-97.76, 26.53) * mm, "mid": v(-94.66, 31.02) * mm, "end": v(-91.46, 35.46) * mm});
            skArc(sketch, "E297", {"start": v(-91.46, 35.46) * mm, "mid": v(-90.3, 36.46) * mm, "end": v(-88.8, 36.85) * mm});
            skArc(sketch, "E298", {"start": v(-88.8, 36.85) * mm, "mid": v(-87.85, 36.4) * mm, "end": v(-87.66, 35.36) * mm});
            skArc(sketch, "E299", {"start": v(-87.66, 35.36) * mm, "mid": v(-89.02, 31.03) * mm, "end": v(-90.5, 26.74) * mm});
            skArc(sketch, "E300", {"start": v(-90.5, 26.74) * mm, "mid": v(-91.56, 23.77) * mm, "end": v(-92.55, 20.8) * mm});
            skArc(sketch, "E301", {"start": v(-92.55, 20.8) * mm, "mid": v(-93.1, 18.9) * mm, "end": v(-93.51, 16.96) * mm});
            skArc(sketch, "E302", {"start": v(-93.51, 16.96) * mm, "mid": v(-93.7, 15.52) * mm, "end": v(-93.72, 14.08) * mm});
            skArc(sketch, "E303", {"start": v(-93.72, 14.08) * mm, "mid": v(-93.57, 12.77) * mm, "end": v(-93.24, 11.5) * mm});
            skArc(sketch, "E304", {"start": v(-93.24, 11.5) * mm, "mid": v(-92.87, 10.73) * mm, "end": v(-92.3, 10.08) * mm});
            skArc(sketch, "E305", {"start": v(-92.3, 10.08) * mm, "mid": v(-91.6, 9.6) * mm, "end": v(-90.8, 9.34) * mm});
            skArc(sketch, "E306", {"start": v(-90.8, 9.34) * mm, "mid": v(-89.81, 9.27) * mm, "end": v(-88.84, 9.4) * mm});
            skArc(sketch, "E307", {"start": v(-88.84, 9.4) * mm, "mid": v(-87.7, 9.76) * mm, "end": v(-86.6, 10.26) * mm});
            skArc(sketch, "E308", {"start": v(-86.6, 10.26) * mm, "mid": v(-86.05, 10.63) * mm, "end": v(-85.57, 11.09) * mm});
            skArc(sketch, "E309", {"start": v(-85.57, 11.09) * mm, "mid": v(-84.52, 12.33) * mm, "end": v(-83.49, 13.58) * mm});
            skArc(sketch, "E310", {"start": v(-83.49, 13.58) * mm, "mid": v(-82.28, 15.12) * mm, "end": v(-81.1, 16.68) * mm});
            skArc(sketch, "E311", {"start": v(-81.1, 16.68) * mm, "mid": v(-79.85, 18.41) * mm, "end": v(-78.63, 20.16) * mm});
            skArc(sketch, "E312", {"start": v(-78.63, 20.16) * mm, "mid": v(-76.18, 23.62) * mm, "end": v(-73.62, 27) * mm});
            skArc(sketch, "E313", {"start": v(-73.62, 27) * mm, "mid": v(-70.54, 30.82) * mm, "end": v(-67.39, 34.58) * mm});
            skArc(sketch, "E314", {"start": v(-67.39, 34.58) * mm, "mid": v(-64.23, 38.25) * mm, "end": v(-61.04, 41.9) * mm});
            skArc(sketch, "E315", {"start": v(-61.04, 41.9) * mm, "mid": v(-60.52, 42.15) * mm, "end": v(-59.98, 41.94) * mm});
            skArc(sketch, "E316", {"start": v(-59.98, 41.94) * mm, "mid": v(-59.9, 41.78) * mm, "end": v(-59.9, 41.6) * mm});
            skArc(sketch, "E317", {"start": v(-59.9, 41.6) * mm, "mid": v(-60.34, 40.5) * mm, "end": v(-60.77, 39.4) * mm});
            skArc(sketch, "E318", {"start": v(-60.77, 39.4) * mm, "mid": v(-61.3, 38.12) * mm, "end": v(-61.86, 36.84) * mm});
            skArc(sketch, "E319", {"start": v(-61.86, 36.84) * mm, "mid": v(-62.54, 35.35) * mm, "end": v(-63.23, 33.87) * mm});
            skArc(sketch, "E320", {"start": v(-63.23, 33.87) * mm, "mid": v(-64.66, 30.66) * mm, "end": v(-65.94, 27.39) * mm});
            skArc(sketch, "E321", {"start": v(-65.94, 27.39) * mm, "mid": v(-66.75, 24.77) * mm, "end": v(-67.3, 22.1) * mm});
            skArc(sketch, "E322", {"start": v(-67.3, 22.1) * mm, "mid": v(-67.47, 20.05) * mm, "end": v(-67.37, 18) * mm});
            skArc(sketch, "E323", {"start": v(-67.37, 18) * mm, "mid": v(-66.95, 16.52) * mm, "end": v(-66.1, 15.23) * mm});
            skArc(sketch, "E324", {"start": v(-66.1, 15.23) * mm, "mid": v(-65.72, 14.83) * mm, "end": v(-65.31, 14.47) * mm});
            skArc(sketch, "E325", {"start": v(-65.31, 14.47) * mm, "mid": v(-64.88, 14.14) * mm, "end": v(-64.42, 13.83) * mm});
            skArc(sketch, "E326", {"start": v(-64.42, 13.83) * mm, "mid": v(-64, 13.6) * mm, "end": v(-63.55, 13.39) * mm});
            skArc(sketch, "E327", {"start": v(-63.55, 13.39) * mm, "mid": v(-63.22, 13.29) * mm, "end": v(-62.87, 13.25) * mm});
            skArc(sketch, "E328", {"start": v(-62.87, 13.25) * mm, "mid": v(-61.4, 13.42) * mm, "end": v(-60, 13.9) * mm});
            skArc(sketch, "E329", {"start": v(-60, 13.9) * mm, "mid": v(-58.06, 14.91) * mm, "end": v(-56.2, 16.07) * mm});
            skArc(sketch, "E330", {"start": v(-56.2, 16.07) * mm, "mid": v(-53.84, 17.74) * mm, "end": v(-51.58, 19.54) * mm});
            skArc(sketch, "E331", {"start": v(-51.58, 19.54) * mm, "mid": v(-48.8, 21.95) * mm, "end": v(-46.1, 24.44) * mm});
            skLineSegment(sketch, "E332", {"start": v(-46.1, 24.44) * mm, "end": v(-37.8, 32.3) * mm});
            skLineSegment(sketch, "E333", {"start": v(-37.8, 32.3) * mm, "end": v(-36.6, 28.53) * mm});
            skArc(sketch, "E334", {"start": v(-36.6, 28.53) * mm, "mid": v(-35.47, 25.8) * mm, "end": v(-33.91, 23.3) * mm});
            skArc(sketch, "E335", {"start": v(-33.91, 23.3) * mm, "mid": v(-32.07, 21.28) * mm, "end": v(-29.86, 19.68) * mm});
            skArc(sketch, "E336", {"start": v(-29.86, 19.68) * mm, "mid": v(-27.37, 18.56) * mm, "end": v(-24.71, 17.99) * mm});
            skArc(sketch, "E337", {"start": v(-24.71, 17.99) * mm, "mid": v(-21.78, 17.9) * mm, "end": v(-18.87, 18.3) * mm});
            skArc(sketch, "E338", {"start": v(-18.87, 18.3) * mm, "mid": v(-16.52, 18.92) * mm, "end": v(-14.23, 19.7) * mm});
            skArc(sketch, "E339", {"start": v(-14.23, 19.7) * mm, "mid": v(-12, 20.65) * mm, "end": v(-9.85, 21.76) * mm});
            skArc(sketch, "E340", {"start": v(-9.85, 21.76) * mm, "mid": v(-7.52, 23.16) * mm, "end": v(-5.28, 24.71) * mm});
            skArc(sketch, "E341", {"start": v(-5.28, 24.71) * mm, "mid": v(-2.62, 26.75) * mm, "end": v(-0.02, 28.88) * mm});
            skArc(sketch, "E342", {"start": v(-0.02, 28.88) * mm, "mid": v(1.24, 29.93) * mm, "end": v(2.5, 30.98) * mm});
            skArc(sketch, "E343", {"start": v(2.5, 30.98) * mm, "mid": v(3.59, 31.85) * mm, "end": v(4.68, 32.7) * mm});
            skArc(sketch, "E344", {"start": v(4.68, 32.7) * mm, "mid": v(5.61, 33.41) * mm, "end": v(6.55, 34.12) * mm});
            skArc(sketch, "E345", {"start": v(6.55, 34.12) * mm, "mid": v(6.67, 34.16) * mm, "end": v(6.78, 34.1) * mm});
            skArc(sketch, "E346", {"start": v(6.78, 34.1) * mm, "mid": v(6.86, 33.97) * mm, "end": v(6.92, 33.84) * mm});
            skArc(sketch, "E347", {"start": v(6.92, 33.84) * mm, "mid": v(7.12, 33.38) * mm, "end": v(7.32, 32.93) * mm});
            skArc(sketch, "E348", {"start": v(7.32, 32.93) * mm, "mid": v(7.56, 32.38) * mm, "end": v(7.78, 31.83) * mm});
            skArc(sketch, "E349", {"start": v(7.78, 31.83) * mm, "mid": v(8.03, 31.22) * mm, "end": v(8.28, 30.6) * mm});
            skArc(sketch, "E350", {"start": v(8.28, 30.6) * mm, "mid": v(10, 27.5) * mm, "end": v(12.46, 24.96) * mm});
            skArc(sketch, "E351", {"start": v(12.46, 24.96) * mm, "mid": v(15.23, 23.47) * mm, "end": v(18.35, 23.06) * mm});
            skArc(sketch, "E352", {"start": v(18.35, 23.06) * mm, "mid": v(22.62, 23.75) * mm, "end": v(26.65, 25.3) * mm});
            skArc(sketch, "E353", {"start": v(26.65, 25.3) * mm, "mid": v(32.61, 28.6) * mm, "end": v(38.37, 32.22) * mm});
            skArc(sketch, "E354", {"start": v(38.37, 32.22) * mm, "mid": v(41.16, 34.08) * mm, "end": v(43.94, 35.93) * mm});
            skArc(sketch, "E355", {"start": v(43.94, 35.93) * mm, "mid": v(44.7, 36.4) * mm, "end": v(45.5, 36.8) * mm});
            skArc(sketch, "E356", {"start": v(45.5, 36.8) * mm, "mid": v(45.74, 36.79) * mm, "end": v(45.84, 36.57) * mm});
            skArc(sketch, "E357", {"start": v(45.84, 36.57) * mm, "mid": v(45.74, 36.08) * mm, "end": v(45.54, 35.62) * mm});
            skArc(sketch, "E358", {"start": v(45.54, 35.62) * mm, "mid": v(43.76, 32.58) * mm, "end": v(41.8, 29.64) * mm});
            skArc(sketch, "E359", {"start": v(41.8, 29.64) * mm, "mid": v(39.76, 26.97) * mm, "end": v(37.55, 24.44) * mm});
            skArc(sketch, "E360", {"start": v(37.55, 24.44) * mm, "mid": v(35.14, 22) * mm, "end": v(32.57, 19.74) * mm});
            skArc(sketch, "E361", {"start": v(32.57, 19.74) * mm, "mid": v(29.65, 17.45) * mm, "end": v(26.6, 15.3) * mm});
            skArc(sketch, "E362", {"start": v(26.6, 15.3) * mm, "mid": v(22.2, 12.14) * mm, "end": v(18.01, 8.7) * mm});
            skArc(sketch, "E363", {"start": v(18.01, 8.7) * mm, "mid": v(14.66, 5.46) * mm, "end": v(11.65, 1.9) * mm});
            skArc(sketch, "E364", {"start": v(11.65, 1.9) * mm, "mid": v(9.7, -1.07) * mm, "end": v(8.13, -4.25) * mm});
            skArc(sketch, "E365", {"start": v(8.13, -4.25) * mm, "mid": v(7.74, -6.51) * mm, "end": v(8.36, -8.72) * mm});
            skArc(sketch, "E366", {"start": v(8.36, -8.72) * mm, "mid": v(8.66, -9.22) * mm, "end": v(9.02, -9.68) * mm});
            skArc(sketch, "E367", {"start": v(9.02, -9.68) * mm, "mid": v(9.34, -9.94) * mm, "end": v(9.72, -10.1) * mm});
            skArc(sketch, "E368", {"start": v(9.72, -10.1) * mm, "mid": v(10.2, -10.16) * mm, "end": v(10.67, -10.1) * mm});
            skArc(sketch, "E369", {"start": v(10.67, -10.1) * mm, "mid": v(11.47, -9.9) * mm, "end": v(12.25, -9.64) * mm});
            skArc(sketch, "E370", {"start": v(12.25, -9.64) * mm, "mid": v(14.37, -8.71) * mm, "end": v(16.31, -7.47) * mm});
            skArc(sketch, "E371", {"start": v(16.31, -7.47) * mm, "mid": v(19.41, -5.05) * mm, "end": v(22.42, -2.52) * mm});
            skArc(sketch, "E372", {"start": v(22.42, -2.52) * mm, "mid": v(25.76, 0.5) * mm, "end": v(28.98, 3.63) * mm});
            skArc(sketch, "E373", {"start": v(28.98, 3.63) * mm, "mid": v(32.02, 6.8) * mm, "end": v(34.94, 10.1) * mm});
            skArc(sketch, "E374", {"start": v(34.94, 10.1) * mm, "mid": v(37.17, 12.65) * mm, "end": v(39.48, 15.12) * mm});
            skArc(sketch, "E375", {"start": v(39.48, 15.12) * mm, "mid": v(41.18, 16.73) * mm, "end": v(43.01, 18.17) * mm});
            skArc(sketch, "E376", {"start": v(43.01, 18.17) * mm, "mid": v(45.31, 19.71) * mm, "end": v(47.7, 21.1) * mm});
            skArc(sketch, "E377", {"start": v(47.7, 21.1) * mm, "mid": v(52.73, 23.8) * mm, "end": v(57.78, 26.44) * mm});
            skArc(sketch, "E378", {"start": v(57.78, 26.44) * mm, "mid": v(61.02, 28.15) * mm, "end": v(64.24, 29.89) * mm});
            skArc(sketch, "E379", {"start": v(64.24, 29.89) * mm, "mid": v(67.35, 31.6) * mm, "end": v(70.43, 33.37) * mm});
            skArc(sketch, "E380", {"start": v(70.43, 33.37) * mm, "mid": v(73.05, 34.9) * mm, "end": v(75.64, 36.46) * mm});
            skArc(sketch, "E381", {"start": v(75.64, 36.46) * mm, "mid": v(77.03, 37.37) * mm, "end": v(78.36, 38.35) * mm});
            skArc(sketch, "E382", {"start": v(78.36, 38.35) * mm, "mid": v(79.83, 39.47) * mm, "end": v(81.34, 40.53) * mm});
            skArc(sketch, "E383", {"start": v(81.34, 40.53) * mm, "mid": v(82.24, 41.04) * mm, "end": v(83.22, 41.4) * mm});
            skArc(sketch, "E384", {"start": v(83.22, 41.4) * mm, "mid": v(84.3, 41.6) * mm, "end": v(85.4, 41.63) * mm});
            skArc(sketch, "E385", {"start": v(85.4, 41.63) * mm, "mid": v(87.55, 41.51) * mm, "end": v(89.7, 41.35) * mm});
            skLineSegment(sketch, "E386", {"start": v(89.7, 41.35) * mm, "end": v(96.48, 40.75) * mm});
            skLineSegment(sketch, "E387", {"start": v(96.48, 40.75) * mm, "end": v(90.91, 36.75) * mm});
            skArc(sketch, "E388", {"start": v(90.91, 36.75) * mm, "mid": v(87.5, 34.04) * mm, "end": v(84.39, 31) * mm});
            skArc(sketch, "E389", {"start": v(84.39, 31) * mm, "mid": v(82.29, 28.25) * mm, "end": v(80.76, 25.15) * mm});
            skArc(sketch, "E390", {"start": v(80.76, 25.15) * mm, "mid": v(80.17, 22.51) * mm, "end": v(80.34, 19.82) * mm});
            skArc(sketch, "E391", {"start": v(80.34, 19.82) * mm, "mid": v(81.26, 17.43) * mm, "end": v(82.9, 15.47) * mm});
            skArc(sketch, "E392", {"start": v(82.9, 15.47) * mm, "mid": v(83.7, 14.84) * mm, "end": v(84.52, 14.27) * mm});
            skArc(sketch, "E393", {"start": v(84.52, 14.27) * mm, "mid": v(85.18, 13.92) * mm, "end": v(85.9, 13.68) * mm});
            skArc(sketch, "E394", {"start": v(85.9, 13.68) * mm, "mid": v(86.68, 13.55) * mm, "end": v(87.47, 13.54) * mm});
            skArc(sketch, "E395", {"start": v(87.47, 13.54) * mm, "mid": v(88.62, 13.64) * mm, "end": v(89.76, 13.8) * mm});
            skArc(sketch, "E396", {"start": v(89.76, 13.8) * mm, "mid": v(91.42, 14.12) * mm, "end": v(93.05, 14.58) * mm});
            skArc(sketch, "E397", {"start": v(93.05, 14.58) * mm, "mid": v(95.92, 15.5) * mm, "end": v(98.77, 16.48) * mm});
            skArc(sketch, "E398", {"start": v(98.77, 16.48) * mm, "mid": v(101.81, 17.57) * mm, "end": v(104.84, 18.72) * mm});
            skArc(sketch, "E399", {"start": v(104.84, 18.72) * mm, "mid": v(107.4, 19.74) * mm, "end": v(109.92, 20.84) * mm});
            skArc(sketch, "E400", {"start": v(109.92, 20.84) * mm, "mid": v(110.15, 20.86) * mm, "end": v(110.35, 20.74) * mm});
            skArc(sketch, "E401", {"start": v(110.35, 20.74) * mm, "mid": v(110.57, 20.44) * mm, "end": v(110.74, 20.1) * mm});
            skArc(sketch, "E402", {"start": v(110.74, 20.1) * mm, "mid": v(110.92, 19.56) * mm, "end": v(111.04, 19) * mm});
            skArc(sketch, "E403", {"start": v(111.04, 19) * mm, "mid": v(111.15, 18.27) * mm, "end": v(111.22, 17.54) * mm});
            skArc(sketch, "E404", {"start": v(111.22, 17.54) * mm, "mid": v(111.68, 14.67) * mm, "end": v(112.65, 11.93) * mm});
            skArc(sketch, "E405", {"start": v(112.65, 11.93) * mm, "mid": v(114.1, 9.46) * mm, "end": v(115.99, 7.32) * mm});
            skArc(sketch, "E406", {"start": v(115.99, 7.32) * mm, "mid": v(118.25, 5.58) * mm, "end": v(120.81, 4.3) * mm});
            skArc(sketch, "E407", {"start": v(120.81, 4.3) * mm, "mid": v(123.61, 3.52) * mm, "end": v(126.51, 3.25) * mm});
            skArc(sketch, "E408", {"start": v(126.51, 3.25) * mm, "mid": v(127.61, 3.28) * mm, "end": v(128.7, 3.38) * mm});
            skArc(sketch, "E409", {"start": v(128.7, 3.38) * mm, "mid": v(130.02, 3.56) * mm, "end": v(131.33, 3.78) * mm});
            skArc(sketch, "E410", {"start": v(131.33, 3.78) * mm, "mid": v(132.64, 4.05) * mm, "end": v(133.94, 4.36) * mm});
            skArc(sketch, "E411", {"start": v(133.94, 4.36) * mm, "mid": v(135.04, 4.67) * mm, "end": v(136.11, 5.05) * mm});
            skArc(sketch, "E412", {"start": v(136.11, 5.05) * mm, "mid": v(137.45, 5.52) * mm, "end": v(138.81, 5.95) * mm});
            skArc(sketch, "E413", {"start": v(138.81, 5.95) * mm, "mid": v(139.76, 6.18) * mm, "end": v(140.74, 6.3) * mm});
            skArc(sketch, "E414", {"start": v(140.74, 6.3) * mm, "mid": v(141.65, 6.3) * mm, "end": v(142.56, 6.2) * mm});
            skArc(sketch, "E415", {"start": v(142.56, 6.2) * mm, "mid": v(143.72, 5.96) * mm, "end": v(144.87, 5.65) * mm});
            skArc(sketch, "E416", {"start": v(144.87, 5.65) * mm, "mid": v(145.8, 5.41) * mm, "end": v(146.72, 5.23) * mm});
            skArc(sketch, "E417", {"start": v(146.72, 5.23) * mm, "mid": v(147.85, 5.08) * mm, "end": v(148.98, 4.97) * mm});
            skArc(sketch, "E418", {"start": v(148.98, 4.97) * mm, "mid": v(150.13, 4.9) * mm, "end": v(151.28, 4.88) * mm});
            skArc(sketch, "E419", {"start": v(151.28, 4.88) * mm, "mid": v(152.26, 4.92) * mm, "end": v(153.24, 5) * mm});
            skArc(sketch, "E420", {"start": v(153.24, 5) * mm, "mid": v(154.59, 5.17) * mm, "end": v(155.94, 5.3) * mm});
            skArc(sketch, "E421", {"start": v(155.94, 5.3) * mm, "mid": v(156.4, 5.29) * mm, "end": v(156.86, 5.16) * mm});
            skArc(sketch, "E422", {"start": v(156.86, 5.16) * mm, "mid": v(157.1, 4.95) * mm, "end": v(157.17, 4.64) * mm});
            skArc(sketch, "E423", {"start": v(157.17, 4.64) * mm, "mid": v(157.09, 4.04) * mm, "end": v(156.94, 3.45) * mm});
            skArc(sketch, "E424", {"start": v(156.94, 3.45) * mm, "mid": v(156.67, 2.13) * mm, "end": v(156.7, 0.78) * mm});
            skArc(sketch, "E425", {"start": v(156.7, 0.78) * mm, "mid": v(157, -1.07) * mm, "end": v(157.47, -2.9) * mm});
            skArc(sketch, "E426", {"start": v(157.47, -2.9) * mm, "mid": v(158.12, -4.77) * mm, "end": v(158.92, -6.6) * mm});
            skArc(sketch, "E427", {"start": v(158.92, -6.6) * mm, "mid": v(159.76, -8.08) * mm, "end": v(160.8, -9.45) * mm});
            skArc(sketch, "E428", {"start": v(160.8, -9.45) * mm, "mid": v(161.98, -10.54) * mm, "end": v(163.38, -11.33) * mm});
            skArc(sketch, "E429", {"start": v(163.38, -11.33) * mm, "mid": v(165.02, -11.84) * mm, "end": v(166.73, -12.03) * mm});
            skArc(sketch, "E430", {"start": v(166.73, -12.03) * mm, "mid": v(169.1, -11.93) * mm, "end": v(171.45, -11.55) * mm});
            skArc(sketch, "E431", {"start": v(171.45, -11.55) * mm, "mid": v(175.03, -10.7) * mm, "end": v(178.58, -9.74) * mm});
            skArc(sketch, "E432", {"start": v(178.58, -9.74) * mm, "mid": v(180.05, -9.31) * mm, "end": v(181.51, -8.89) * mm});
            skArc(sketch, "E433", {"start": v(181.51, -8.89) * mm, "mid": v(182.9, -8.48) * mm, "end": v(184.28, -8.08) * mm});
            skArc(sketch, "E434", {"start": v(184.28, -8.08) * mm, "mid": v(185.45, -7.74) * mm, "end": v(186.62, -7.4) * mm});
            skArc(sketch, "E435", {"start": v(186.62, -7.4) * mm, "mid": v(187.18, -7.24) * mm, "end": v(187.75, -7.08) * mm});
            skArc(sketch, "E436", {"start": v(187.75, -7.08) * mm, "mid": v(188.09, -7.04) * mm, "end": v(188.42, -7.13) * mm});
            skArc(sketch, "E437", {"start": v(188.42, -7.13) * mm, "mid": v(188.6, -7.31) * mm, "end": v(188.61, -7.57) * mm});
            skArc(sketch, "E438", {"start": v(188.61, -7.57) * mm, "mid": v(188.37, -8.17) * mm, "end": v(188.05, -8.74) * mm});
            skArc(sketch, "E439", {"start": v(188.05, -8.74) * mm, "mid": v(187.22, -10) * mm, "end": v(186.37, -11.25) * mm});
            skArc(sketch, "E440", {"start": v(186.37, -11.25) * mm, "mid": v(184.72, -14.02) * mm, "end": v(183.46, -16.99) * mm});
            skArc(sketch, "E441", {"start": v(183.46, -16.99) * mm, "mid": v(183.17, -19.14) * mm, "end": v(183.75, -21.22) * mm});
            skArc(sketch, "E442", {"start": v(183.75, -21.22) * mm, "mid": v(185.1, -22.9) * mm, "end": v(187.02, -23.89) * mm});
            skArc(sketch, "E443", {"start": v(187.02, -23.89) * mm, "mid": v(190.14, -24.53) * mm, "end": v(193.32, -24.75) * mm});
            skArc(sketch, "E444", {"start": v(193.32, -24.75) * mm, "mid": v(194.62, -24.73) * mm, "end": v(195.92, -24.67) * mm});
            skArc(sketch, "E445", {"start": v(195.92, -24.67) * mm, "mid": v(197.48, -24.55) * mm, "end": v(199.04, -24.41) * mm});
            skArc(sketch, "E446", {"start": v(199.04, -24.41) * mm, "mid": v(200.6, -24.24) * mm, "end": v(202.15, -24.04) * mm});
            skArc(sketch, "E447", {"start": v(202.15, -24.04) * mm, "mid": v(203.46, -23.84) * mm, "end": v(204.76, -23.6) * mm});
            skLineSegment(sketch, "E448", {"start": v(204.76, -23.6) * mm, "end": v(210.47, -22.45) * mm});
            skLineSegment(sketch, "E449", {"start": v(210.47, -22.45) * mm, "end": v(213.87, -25.74) * mm});
            skArc(sketch, "E450", {"start": v(213.87, -25.74) * mm, "mid": v(214.82, -26.6) * mm, "end": v(215.82, -27.4) * mm});
            skArc(sketch, "E451", {"start": v(215.82, -27.4) * mm, "mid": v(216.68, -27.99) * mm, "end": v(217.61, -28.47) * mm});
            skArc(sketch, "E452", {"start": v(217.61, -28.47) * mm, "mid": v(218.62, -28.85) * mm, "end": v(219.66, -29.12) * mm});
            skArc(sketch, "E453", {"start": v(219.66, -29.12) * mm, "mid": v(221.02, -29.36) * mm, "end": v(222.4, -29.52) * mm});
            skArc(sketch, "E454", {"start": v(222.4, -29.52) * mm, "mid": v(224.04, -29.7) * mm, "end": v(225.68, -29.9) * mm});
            skArc(sketch, "E455", {"start": v(225.68, -29.9) * mm, "mid": v(226.23, -30.03) * mm, "end": v(226.73, -30.3) * mm});
            skArc(sketch, "E456", {"start": v(226.73, -30.3) * mm, "mid": v(227, -30.63) * mm, "end": v(227.06, -31.05) * mm});
            skArc(sketch, "E457", {"start": v(227.06, -31.05) * mm, "mid": v(226.94, -31.85) * mm, "end": v(226.75, -32.63) * mm});
            skArc(sketch, "E458", {"start": v(226.75, -32.63) * mm, "mid": v(226.58, -33.29) * mm, "end": v(226.45, -33.95) * mm});
            skArc(sketch, "E459", {"start": v(226.45, -33.95) * mm, "mid": v(226.3, -34.87) * mm, "end": v(226.2, -35.8) * mm});
            skArc(sketch, "E460", {"start": v(226.2, -35.8) * mm, "mid": v(226.08, -36.82) * mm, "end": v(226, -37.83) * mm});
            skArc(sketch, "E461", {"start": v(226, -37.83) * mm, "mid": v(225.95, -38.8) * mm, "end": v(225.93, -39.75) * mm});
            skArc(sketch, "E462", {"start": v(225.93, -39.75) * mm, "mid": v(225.93, -41.1) * mm, "end": v(225.97, -42.43) * mm});
            skArc(sketch, "E463", {"start": v(225.97, -42.43) * mm, "mid": v(226.07, -43.03) * mm, "end": v(226.3, -43.6) * mm});
            skArc(sketch, "E464", {"start": v(226.3, -43.6) * mm, "mid": v(226.6, -43.98) * mm, "end": v(227.03, -44.22) * mm});
            skArc(sketch, "E465", {"start": v(227.03, -44.22) * mm, "mid": v(227.78, -44.43) * mm, "end": v(228.54, -44.56) * mm});
            skArc(sketch, "E466", {"start": v(228.54, -44.56) * mm, "mid": v(229.28, -44.6) * mm, "end": v(230.03, -44.58) * mm});
            skArc(sketch, "E467", {"start": v(230.03, -44.58) * mm, "mid": v(231.33, -44.46) * mm, "end": v(232.64, -44.32) * mm});
            skArc(sketch, "E468", {"start": v(232.64, -44.32) * mm, "mid": v(234.15, -44.11) * mm, "end": v(235.66, -43.88) * mm});
            skArc(sketch, "E469", {"start": v(235.66, -43.88) * mm, "mid": v(237.2, -43.6) * mm, "end": v(238.75, -43.3) * mm});
            skArc(sketch, "E470", {"start": v(238.75, -43.3) * mm, "mid": v(242.1, -42.72) * mm, "end": v(245.47, -42.34) * mm});
            skArc(sketch, "E471", {"start": v(245.47, -42.34) * mm, "mid": v(249.9, -42.05) * mm, "end": v(254.35, -41.87) * mm});
            skArc(sketch, "E472", {"start": v(254.35, -41.87) * mm, "mid": v(258.62, -41.81) * mm, "end": v(262.88, -41.85) * mm});
            skArc(sketch, "E473", {"start": v(262.88, -41.85) * mm, "mid": v(264.82, -42.05) * mm, "end": v(266.7, -42.6) * mm});
            skArc(sketch, "E474", {"start": v(266.7, -42.6) * mm, "mid": v(266.88, -42.77) * mm, "end": v(266.93, -43.02) * mm});
            skArc(sketch, "E475", {"start": v(266.93, -43.02) * mm, "mid": v(266.83, -43.28) * mm, "end": v(266.61, -43.45) * mm});
            skArc(sketch, "E476", {"start": v(266.61, -43.45) * mm, "mid": v(265.88, -43.75) * mm, "end": v(265.13, -43.97) * mm});
            skArc(sketch, "E477", {"start": v(265.13, -43.97) * mm, "mid": v(263.71, -44.3) * mm, "end": v(262.3, -44.6) * mm});
            skArc(sketch, "E478", {"start": v(262.3, -44.6) * mm, "mid": v(260.9, -44.9) * mm, "end": v(259.52, -45.24) * mm});
            skArc(sketch, "E479", {"start": v(259.52, -45.24) * mm, "mid": v(257.92, -45.66) * mm, "end": v(256.32, -46.1) * mm});
            skArc(sketch, "E480", {"start": v(256.32, -46.1) * mm, "mid": v(254.76, -46.56) * mm, "end": v(253.21, -47.03) * mm});
            skArc(sketch, "E481", {"start": v(253.21, -47.03) * mm, "mid": v(251.95, -47.45) * mm, "end": v(250.7, -47.9) * mm});
            skArc(sketch, "E482", {"start": v(250.7, -47.9) * mm, "mid": v(247.84, -49.25) * mm, "end": v(245.23, -51.05) * mm});
            skArc(sketch, "E483", {"start": v(245.23, -51.05) * mm, "mid": v(243.65, -52.9) * mm, "end": v(242.8, -55.19) * mm});
            skArc(sketch, "E484", {"start": v(242.8, -55.19) * mm, "mid": v(242.88, -57.34) * mm, "end": v(243.86, -59.26) * mm});
            skArc(sketch, "E485", {"start": v(243.86, -59.26) * mm, "mid": v(245.77, -61.09) * mm, "end": v(248.07, -62.4) * mm});
            skArc(sketch, "E486", {"start": v(248.07, -62.4) * mm, "mid": v(250.82, -63.33) * mm, "end": v(253.67, -63.9) * mm});
            skArc(sketch, "E487", {"start": v(253.67, -63.9) * mm, "mid": v(259.16, -64.55) * mm, "end": v(264.66, -65.07) * mm});
            skArc(sketch, "E488", {"start": v(264.66, -65.07) * mm, "mid": v(270.38, -65.5) * mm, "end": v(276.11, -65.88) * mm});
            skArc(sketch, "E489", {"start": v(276.11, -65.88) * mm, "mid": v(277.45, -65.67) * mm, "end": v(278.59, -64.94) * mm});
            skArc(sketch, "E490", {"start": v(278.59, -64.94) * mm, "mid": v(278.94, -64.39) * mm, "end": v(279.03, -63.74) * mm});
            skArc(sketch, "E491", {"start": v(279.03, -63.74) * mm, "mid": v(278.83, -63.14) * mm, "end": v(278.38, -62.71) * mm});
            skArc(sketch, "E492", {"start": v(278.38, -62.71) * mm, "mid": v(277.26, -62.17) * mm, "end": v(276.08, -61.8) * mm});
            skArc(sketch, "E493", {"start": v(276.08, -61.8) * mm, "mid": v(273.74, -61.26) * mm, "end": v(271.39, -60.79) * mm});
            skArc(sketch, "E494", {"start": v(271.39, -60.79) * mm, "mid": v(268.7, -60.22) * mm, "end": v(266.03, -59.55) * mm});
            skArc(sketch, "E495", {"start": v(266.03, -59.55) * mm, "mid": v(264.12, -58.93) * mm, "end": v(262.29, -58.13) * mm});
            skArc(sketch, "E496", {"start": v(262.29, -58.13) * mm, "mid": v(261.13, -57.45) * mm, "end": v(260.1, -56.59) * mm});
            skArc(sketch, "E497", {"start": v(260.1, -56.59) * mm, "mid": v(259.63, -55.83) * mm, "end": v(259.57, -54.95) * mm});
            skArc(sketch, "E498", {"start": v(259.57, -54.95) * mm, "mid": v(260.03, -53.83) * mm, "end": v(260.88, -52.97) * mm});
            skArc(sketch, "E499", {"start": v(260.88, -52.97) * mm, "mid": v(262.29, -52.17) * mm, "end": v(263.81, -51.63) * mm});
            skArc(sketch, "E500", {"start": v(263.81, -51.63) * mm, "mid": v(266.17, -51.12) * mm, "end": v(268.57, -50.85) * mm});
            skArc(sketch, "E501", {"start": v(268.57, -50.85) * mm, "mid": v(272.12, -50.7) * mm, "end": v(275.66, -50.65) * mm});
            skArc(sketch, "E502", {"start": v(275.66, -50.65) * mm, "mid": v(277.66, -50.65) * mm, "end": v(279.65, -50.62) * mm});
            skArc(sketch, "E503", {"start": v(279.65, -50.62) * mm, "mid": v(281.43, -50.57) * mm, "end": v(283.2, -50.48) * mm});
            skArc(sketch, "E504", {"start": v(283.2, -50.48) * mm, "mid": v(284.67, -50.38) * mm, "end": v(286.15, -50.26) * mm});
            skArc(sketch, "E505", {"start": v(286.15, -50.26) * mm, "mid": v(286.58, -50.17) * mm, "end": v(286.97, -49.98) * mm});
            skArc(sketch, "E506", {"start": v(286.97, -49.98) * mm, "mid": v(287.62, -49.45) * mm, "end": v(288.16, -48.81) * mm});
            skArc(sketch, "E507", {"start": v(288.16, -48.81) * mm, "mid": v(288.76, -47.87) * mm, "end": v(289.28, -46.88) * mm});
            skArc(sketch, "E508", {"start": v(289.28, -46.88) * mm, "mid": v(289.74, -45.82) * mm, "end": v(290.1, -44.72) * mm});
            skArc(sketch, "E509", {"start": v(290.1, -44.72) * mm, "mid": v(290.3, -43.79) * mm, "end": v(290.37, -42.84) * mm});
            skArc(sketch, "E510", {"start": v(290.37, -42.84) * mm, "mid": v(289.75, -40.7) * mm, "end": v(288.06, -39.22) * mm});
            skArc(sketch, "E511", {"start": v(288.06, -39.22) * mm, "mid": v(284.25, -37.7) * mm, "end": v(280.29, -36.61) * mm});
            skArc(sketch, "E512", {"start": v(280.29, -36.61) * mm, "mid": v(274.55, -35.62) * mm, "end": v(268.76, -35.1) * mm});
            skArc(sketch, "E513", {"start": v(268.76, -35.1) * mm, "mid": v(261.45, -34.9) * mm, "end": v(254.14, -35) * mm});
            skArc(sketch, "E514", {"start": v(254.14, -35) * mm, "mid": v(250.14, -35.13) * mm, "end": v(246.14, -35.23) * mm});
            skArc(sketch, "E515", {"start": v(246.14, -35.23) * mm, "mid": v(244.14, -35.24) * mm, "end": v(242.15, -35.16) * mm});
            skArc(sketch, "E516", {"start": v(242.15, -35.16) * mm, "mid": v(241.05, -35.05) * mm, "end": v(239.96, -34.84) * mm});
            skArc(sketch, "E517", {"start": v(239.96, -34.84) * mm, "mid": v(239.54, -34.58) * mm, "end": v(239.37, -34.11) * mm});
            skArc(sketch, "E518", {"start": v(239.37, -34.11) * mm, "mid": v(239.58, -33.31) * mm, "end": v(240.15, -32.71) * mm});
            skArc(sketch, "E519", {"start": v(240.15, -32.71) * mm, "mid": v(241.35, -32.07) * mm, "end": v(242.62, -31.58) * mm});
            skArc(sketch, "E520", {"start": v(242.62, -31.58) * mm, "mid": v(244.67, -31.03) * mm, "end": v(246.76, -30.63) * mm});
            skArc(sketch, "E521", {"start": v(246.76, -30.63) * mm, "mid": v(249.92, -30.2) * mm, "end": v(253.1, -29.84) * mm});
            skArc(sketch, "E522", {"start": v(253.1, -29.84) * mm, "mid": v(254.75, -29.65) * mm, "end": v(256.4, -29.43) * mm});
            skArc(sketch, "E523", {"start": v(256.4, -29.43) * mm, "mid": v(257.89, -29.2) * mm, "end": v(259.36, -28.93) * mm});
            skArc(sketch, "E524", {"start": v(259.36, -28.93) * mm, "mid": v(260.57, -28.68) * mm, "end": v(261.77, -28.4) * mm});
            skArc(sketch, "E525", {"start": v(261.77, -28.4) * mm, "mid": v(262.2, -28.24) * mm, "end": v(262.56, -27.96) * mm});
            skArc(sketch, "E526", {"start": v(262.56, -27.96) * mm, "mid": v(263.16, -26.84) * mm, "end": v(263.06, -25.57) * mm});
            skArc(sketch, "E527", {"start": v(263.06, -25.57) * mm, "mid": v(262.22, -24.05) * mm, "end": v(261.04, -22.78) * mm});
            skArc(sketch, "E528", {"start": v(261.04, -22.78) * mm, "mid": v(259.16, -21.49) * mm, "end": v(257.1, -20.53) * mm});
            skArc(sketch, "E529", {"start": v(257.1, -20.53) * mm, "mid": v(254.9, -19.95) * mm, "end": v(252.63, -19.75) * mm});
            skArc(sketch, "E530", {"start": v(252.63, -19.75) * mm, "mid": v(250.7, -19.85) * mm, "end": v(248.78, -20.15) * mm});
            skArc(sketch, "E531", {"start": v(248.78, -20.15) * mm, "mid": v(245.31, -20.93) * mm, "end": v(241.87, -21.77) * mm});
            skArc(sketch, "E532", {"start": v(241.87, -21.77) * mm, "mid": v(238.35, -22.7) * mm, "end": v(234.85, -23.65) * mm});
            skArc(sketch, "E533", {"start": v(234.85, -23.65) * mm, "mid": v(233.83, -24.09) * mm, "end": v(232.96, -24.76) * mm});
            skArc(sketch, "E534", {"start": v(232.96, -24.76) * mm, "mid": v(232.16, -25.33) * mm, "end": v(231.2, -25.61) * mm});
            skArc(sketch, "E535", {"start": v(231.2, -25.61) * mm, "mid": v(229.62, -25.73) * mm, "end": v(228.03, -25.7) * mm});
            skArc(sketch, "E536", {"start": v(228.03, -25.7) * mm, "mid": v(226.41, -25.54) * mm, "end": v(224.83, -25.23) * mm});
            skArc(sketch, "E537", {"start": v(224.83, -25.23) * mm, "mid": v(223.81, -24.83) * mm, "end": v(222.95, -24.18) * mm});
            skArc(sketch, "E538", {"start": v(222.95, -24.18) * mm, "mid": v(222.24, -23.35) * mm, "end": v(221.67, -22.42) * mm});
            skArc(sketch, "E539", {"start": v(221.67, -22.42) * mm, "mid": v(221.51, -21.73) * mm, "end": v(221.71, -21.04) * mm});
            skArc(sketch, "E540", {"start": v(221.71, -21.04) * mm, "mid": v(222.3, -20.32) * mm, "end": v(223.06, -19.8) * mm});
            skArc(sketch, "E541", {"start": v(223.06, -19.8) * mm, "mid": v(224.68, -19.1) * mm, "end": v(226.33, -18.46) * mm});
            skArc(sketch, "E542", {"start": v(226.33, -18.46) * mm, "mid": v(228.46, -17.61) * mm, "end": v(230.52, -16.6) * mm});
            skArc(sketch, "E543", {"start": v(230.52, -16.6) * mm, "mid": v(232.33, -15.53) * mm, "end": v(234.03, -14.29) * mm});
            skArc(sketch, "E544", {"start": v(234.03, -14.29) * mm, "mid": v(235.4, -13.04) * mm, "end": v(236.65, -11.65) * mm});
            skArc(sketch, "E545", {"start": v(236.65, -11.65) * mm, "mid": v(237.54, -10.31) * mm, "end": v(238.19, -8.85) * mm});
            skArc(sketch, "E546", {"start": v(238.19, -8.85) * mm, "mid": v(238.5, -7.62) * mm, "end": v(238.62, -6.36) * mm});
            skArc(sketch, "E547", {"start": v(238.62, -6.36) * mm, "mid": v(238.43, -5.5) * mm, "end": v(237.87, -4.81) * mm});
            skArc(sketch, "E548", {"start": v(237.87, -4.81) * mm, "mid": v(236.9, -4.25) * mm, "end": v(235.8, -3.97) * mm});
            skArc(sketch, "E549", {"start": v(235.8, -3.97) * mm, "mid": v(233.76, -3.8) * mm, "end": v(231.71, -3.75) * mm});
            skArc(sketch, "E550", {"start": v(231.71, -3.75) * mm, "mid": v(229, -3.89) * mm, "end": v(226.32, -4.31) * mm});
            skArc(sketch, "E551", {"start": v(226.32, -4.31) * mm, "mid": v(223.43, -5.04) * mm, "end": v(220.6, -6) * mm});
            skArc(sketch, "E552", {"start": v(220.6, -6) * mm, "mid": v(217.98, -7.13) * mm, "end": v(215.45, -8.46) * mm});
            skArc(sketch, "E553", {"start": v(215.45, -8.46) * mm, "mid": v(213.56, -9.76) * mm, "end": v(211.87, -11.33) * mm});
            skArc(sketch, "E554", {"start": v(211.87, -11.33) * mm, "mid": v(211.1, -12.1) * mm, "end": v(210.28, -12.8) * mm});
            skArc(sketch, "E555", {"start": v(210.28, -12.8) * mm, "mid": v(209.38, -13.47) * mm, "end": v(208.43, -14.06) * mm});
            skArc(sketch, "E556", {"start": v(208.43, -14.06) * mm, "mid": v(207.42, -14.6) * mm, "end": v(206.37, -15.06) * mm});
            skArc(sketch, "E557", {"start": v(206.37, -15.06) * mm, "mid": v(205.27, -15.46) * mm, "end": v(204.14, -15.78) * mm});
            skArc(sketch, "E558", {"start": v(204.14, -15.78) * mm, "mid": v(202.37, -16.16) * mm, "end": v(200.58, -16.4) * mm});
            skArc(sketch, "E559", {"start": v(200.58, -16.4) * mm, "mid": v(198.98, -16.47) * mm, "end": v(197.39, -16.36) * mm});
            skArc(sketch, "E560", {"start": v(197.39, -16.36) * mm, "mid": v(196.23, -16.13) * mm, "end": v(195.12, -15.74) * mm});
            skArc(sketch, "E561", {"start": v(195.12, -15.74) * mm, "mid": v(194.58, -15.28) * mm, "end": v(194.37, -14.6) * mm});
            skArc(sketch, "E562", {"start": v(194.37, -14.6) * mm, "mid": v(194.6, -13.54) * mm, "end": v(195.22, -12.65) * mm});
            skArc(sketch, "E563", {"start": v(195.22, -12.65) * mm, "mid": v(197.05, -11) * mm, "end": v(198.95, -9.45) * mm});
            skArc(sketch, "E564", {"start": v(198.95, -9.45) * mm, "mid": v(201.52, -7.55) * mm, "end": v(204.17, -5.78) * mm});
            skArc(sketch, "E565", {"start": v(204.17, -5.78) * mm, "mid": v(207.43, -3.78) * mm, "end": v(210.74, -1.87) * mm});
            skArc(sketch, "E566", {"start": v(210.74, -1.87) * mm, "mid": v(212.6, -0.81) * mm, "end": v(214.43, 0.28) * mm});
            skArc(sketch, "E567", {"start": v(214.43, 0.28) * mm, "mid": v(216, 1.27) * mm, "end": v(217.54, 2.3) * mm});
            skArc(sketch, "E568", {"start": v(217.54, 2.3) * mm, "mid": v(218.79, 3.19) * mm, "end": v(220.02, 4.1) * mm});
            skArc(sketch, "E569", {"start": v(220.02, 4.1) * mm, "mid": v(220.28, 4.4) * mm, "end": v(220.37, 4.8) * mm});
            skArc(sketch, "E570", {"start": v(220.37, 4.8) * mm, "mid": v(220.33, 5.13) * mm, "end": v(220.21, 5.44) * mm});
            skArc(sketch, "E571", {"start": v(220.21, 5.44) * mm, "mid": v(219.95, 5.88) * mm, "end": v(219.65, 6.3) * mm});
            skArc(sketch, "E572", {"start": v(219.65, 6.3) * mm, "mid": v(219.27, 6.76) * mm, "end": v(218.85, 7.2) * mm});
            skArc(sketch, "E573", {"start": v(218.85, 7.2) * mm, "mid": v(218.4, 7.64) * mm, "end": v(217.91, 8.04) * mm});
            skLineSegment(sketch, "E574", {"start": v(217.91, 8.04) * mm, "end": v(215.45, 9.98) * mm});
            skLineSegment(sketch, "E575", {"start": v(215.45, 9.98) * mm, "end": v(196.16, 4.21) * mm});
            skArc(sketch, "E576", {"start": v(196.16, 4.21) * mm, "mid": v(188.61, 1.99) * mm, "end": v(181.05, -0.18) * mm});
            skArc(sketch, "E577", {"start": v(181.05, -0.18) * mm, "mid": v(177.1, -1.2) * mm, "end": v(173.12, -2.04) * mm});
            skArc(sketch, "E578", {"start": v(173.12, -2.04) * mm, "mid": v(170.82, -2.36) * mm, "end": v(168.51, -2.48) * mm});
            skArc(sketch, "E579", {"start": v(168.51, -2.48) * mm, "mid": v(167.44, -2.16) * mm, "end": v(166.75, -1.28) * mm});
            skArc(sketch, "E580", {"start": v(166.75, -1.28) * mm, "mid": v(166.64, -0.86) * mm, "end": v(166.62, -0.43) * mm});
            skArc(sketch, "E581", {"start": v(166.62, -0.43) * mm, "mid": v(166.7, 0.12) * mm, "end": v(166.82, 0.66) * mm});
            skArc(sketch, "E582", {"start": v(166.82, 0.66) * mm, "mid": v(167.04, 1.26) * mm, "end": v(167.3, 1.84) * mm});
            skArc(sketch, "E583", {"start": v(167.3, 1.84) * mm, "mid": v(167.64, 2.42) * mm, "end": v(168.02, 2.98) * mm});
            skArc(sketch, "E584", {"start": v(168.02, 2.98) * mm, "mid": v(168.7, 3.75) * mm, "end": v(169.5, 4.4) * mm});
            skArc(sketch, "E585", {"start": v(169.5, 4.4) * mm, "mid": v(170.51, 5.01) * mm, "end": v(171.58, 5.5) * mm});
            skArc(sketch, "E586", {"start": v(171.58, 5.5) * mm, "mid": v(173.18, 6.08) * mm, "end": v(174.8, 6.56) * mm});
            skArc(sketch, "E587", {"start": v(174.8, 6.56) * mm, "mid": v(177.57, 7.24) * mm, "end": v(180.34, 7.89) * mm});
            skArc(sketch, "E588", {"start": v(180.34, 7.89) * mm, "mid": v(184.45, 8.88) * mm, "end": v(188.53, 10) * mm});
            skArc(sketch, "E589", {"start": v(188.53, 10) * mm, "mid": v(191.63, 11.02) * mm, "end": v(194.66, 12.26) * mm});
            skArc(sketch, "E590", {"start": v(194.66, 12.26) * mm, "mid": v(196.77, 13.31) * mm, "end": v(198.78, 14.55) * mm});
            skArc(sketch, "E591", {"start": v(198.78, 14.55) * mm, "mid": v(199.7, 15.5) * mm, "end": v(200.15, 16.75) * mm});
            skArc(sketch, "E592", {"start": v(200.15, 16.75) * mm, "mid": v(200.06, 17.83) * mm, "end": v(199.54, 18.78) * mm});
            skArc(sketch, "E593", {"start": v(199.54, 18.78) * mm, "mid": v(198.4, 19.96) * mm, "end": v(197.1, 20.98) * mm});
            skArc(sketch, "E594", {"start": v(197.1, 20.98) * mm, "mid": v(195.52, 21.93) * mm, "end": v(193.83, 22.68) * mm});
            skArc(sketch, "E595", {"start": v(193.83, 22.68) * mm, "mid": v(192.28, 23.1) * mm, "end": v(190.67, 23.25) * mm});
            skArc(sketch, "E596", {"start": v(190.67, 23.25) * mm, "mid": v(187.54, 23.03) * mm, "end": v(184.47, 22.37) * mm});
            skArc(sketch, "E597", {"start": v(184.47, 22.37) * mm, "mid": v(179.71, 20.88) * mm, "end": v(175.02, 19.22) * mm});
            skArc(sketch, "E598", {"start": v(175.02, 19.22) * mm, "mid": v(170.43, 17.4) * mm, "end": v(165.92, 15.4) * mm});
            skArc(sketch, "E599", {"start": v(165.92, 15.4) * mm, "mid": v(163.48, 14.01) * mm, "end": v(161.33, 12.21) * mm});
            skArc(sketch, "E600", {"start": v(161.33, 12.21) * mm, "mid": v(160.2, 11.3) * mm, "end": v(158.9, 10.63) * mm});
            skArc(sketch, "E601", {"start": v(158.9, 10.63) * mm, "mid": v(157.05, 10) * mm, "end": v(155.16, 9.56) * mm});
            skArc(sketch, "E602", {"start": v(155.16, 9.56) * mm, "mid": v(153.37, 9.3) * mm, "end": v(151.57, 9.2) * mm});
            skArc(sketch, "E603", {"start": v(151.57, 9.2) * mm, "mid": v(150.67, 9.42) * mm, "end": v(150, 10.06) * mm});
            skArc(sketch, "E604", {"start": v(150, 10.06) * mm, "mid": v(149.9, 10.4) * mm, "end": v(150, 10.72) * mm});
            skArc(sketch, "E605", {"start": v(150, 10.72) * mm, "mid": v(150.54, 11.56) * mm, "end": v(151.12, 12.38) * mm});
            skArc(sketch, "E606", {"start": v(151.12, 12.38) * mm, "mid": v(151.9, 13.38) * mm, "end": v(152.72, 14.35) * mm});
            skArc(sketch, "E607", {"start": v(152.72, 14.35) * mm, "mid": v(153.72, 15.43) * mm, "end": v(154.74, 16.49) * mm});
            skArc(sketch, "E608", {"start": v(154.74, 16.49) * mm, "mid": v(156.74, 18.61) * mm, "end": v(158.6, 20.86) * mm});
            skArc(sketch, "E609", {"start": v(158.6, 20.86) * mm, "mid": v(159.77, 22.64) * mm, "end": v(160.66, 24.57) * mm});
            skArc(sketch, "E610", {"start": v(160.66, 24.57) * mm, "mid": v(161.02, 26.12) * mm, "end": v(161.01, 27.7) * mm});
            skArc(sketch, "E611", {"start": v(161.01, 27.7) * mm, "mid": v(160.61, 29.1) * mm, "end": v(159.81, 30.32) * mm});
            skArc(sketch, "E612", {"start": v(159.81, 30.32) * mm, "mid": v(159.46, 30.73) * mm, "end": v(159.13, 31.16) * mm});
            skArc(sketch, "E613", {"start": v(159.13, 31.16) * mm, "mid": v(158.95, 31.44) * mm, "end": v(158.84, 31.75) * mm});
            skArc(sketch, "E614", {"start": v(158.84, 31.75) * mm, "mid": v(158.83, 31.93) * mm, "end": v(158.92, 32.1) * mm});
            skArc(sketch, "E615", {"start": v(158.92, 32.1) * mm, "mid": v(159.1, 32.21) * mm, "end": v(159.29, 32.25) * mm});
            skArc(sketch, "E616", {"start": v(159.29, 32.25) * mm, "mid": v(159.53, 32.3) * mm, "end": v(159.74, 32.42) * mm});
            skArc(sketch, "E617", {"start": v(159.74, 32.42) * mm, "mid": v(159.93, 32.64) * mm, "end": v(160.07, 32.9) * mm});
            skArc(sketch, "E618", {"start": v(160.07, 32.9) * mm, "mid": v(160.18, 33.25) * mm, "end": v(160.23, 33.62) * mm});
            skArc(sketch, "E619", {"start": v(160.23, 33.62) * mm, "mid": v(160.23, 34.06) * mm, "end": v(160.2, 34.5) * mm});
            skArc(sketch, "E620", {"start": v(160.2, 34.5) * mm, "mid": v(159.78, 35.72) * mm, "end": v(158.95, 36.7) * mm});
            skArc(sketch, "E621", {"start": v(158.95, 36.7) * mm, "mid": v(157.41, 37.81) * mm, "end": v(155.74, 38.73) * mm});
            skArc(sketch, "E622", {"start": v(155.74, 38.73) * mm, "mid": v(153.57, 39.62) * mm, "end": v(151.32, 40.28) * mm});
            skArc(sketch, "E623", {"start": v(151.32, 40.28) * mm, "mid": v(148.82, 40.78) * mm, "end": v(146.3, 41.06) * mm});
            skArc(sketch, "E624", {"start": v(146.3, 41.06) * mm, "mid": v(141.87, 41.12) * mm, "end": v(137.46, 40.64) * mm});
            skArc(sketch, "E625", {"start": v(137.46, 40.64) * mm, "mid": v(132.74, 39.62) * mm, "end": v(128.14, 38.17) * mm});
            skArc(sketch, "E626", {"start": v(128.14, 38.17) * mm, "mid": v(123.92, 36.37) * mm, "end": v(119.88, 34.18) * mm});
            skArc(sketch, "E627", {"start": v(119.88, 34.18) * mm, "mid": v(116.85, 31.97) * mm, "end": v(114.26, 29.26) * mm});
            skArc(sketch, "E628", {"start": v(114.26, 29.26) * mm, "mid": v(113.46, 28.32) * mm, "end": v(112.6, 27.44) * mm});
            skArc(sketch, "E629", {"start": v(112.6, 27.44) * mm, "mid": v(111.78, 26.72) * mm, "end": v(110.9, 26.08) * mm});
            skArc(sketch, "E630", {"start": v(110.9, 26.08) * mm, "mid": v(109.98, 25.53) * mm, "end": v(109.02, 25.07) * mm});
            skArc(sketch, "E631", {"start": v(109.02, 25.07) * mm, "mid": v(107.94, 24.67) * mm, "end": v(106.84, 24.35) * mm});
            skArc(sketch, "E632", {"start": v(106.84, 24.35) * mm, "mid": v(103.67, 23.68) * mm, "end": v(100.46, 23.25) * mm});
            skArc(sketch, "E633", {"start": v(100.46, 23.25) * mm, "mid": v(98.02, 23.24) * mm, "end": v(95.62, 23.65) * mm});
            skArc(sketch, "E634", {"start": v(95.62, 23.65) * mm, "mid": v(94.29, 24.3) * mm, "end": v(93.28, 25.39) * mm});
            skArc(sketch, "E635", {"start": v(93.28, 25.39) * mm, "mid": v(92.9, 26.65) * mm, "end": v(93.21, 27.94) * mm});
            skArc(sketch, "E636", {"start": v(93.21, 27.94) * mm, "mid": v(93.99, 29.17) * mm, "end": v(94.92, 30.3) * mm});
            skArc(sketch, "E637", {"start": v(94.92, 30.3) * mm, "mid": v(96.17, 31.5) * mm, "end": v(97.5, 32.61) * mm});
            skArc(sketch, "E638", {"start": v(97.5, 32.61) * mm, "mid": v(99.29, 33.88) * mm, "end": v(101.14, 35.05) * mm});
            skArc(sketch, "E639", {"start": v(101.14, 35.05) * mm, "mid": v(103.61, 36.45) * mm, "end": v(106.12, 37.78) * mm});
            skArc(sketch, "E640", {"start": v(106.12, 37.78) * mm, "mid": v(108.29, 38.91) * mm, "end": v(110.43, 40.08) * mm});
            skArc(sketch, "E641", {"start": v(110.43, 40.08) * mm, "mid": v(111.38, 40.69) * mm, "end": v(112.25, 41.4) * mm});
            skArc(sketch, "E642", {"start": v(112.25, 41.4) * mm, "mid": v(112.75, 42.02) * mm, "end": v(113.08, 42.75) * mm});
            skArc(sketch, "E643", {"start": v(113.08, 42.75) * mm, "mid": v(113.3, 43.68) * mm, "end": v(113.36, 44.63) * mm});
            skArc(sketch, "E644", {"start": v(113.36, 44.63) * mm, "mid": v(113.34, 45.27) * mm, "end": v(113.3, 45.92) * mm});
            skArc(sketch, "E645", {"start": v(113.3, 45.92) * mm, "mid": v(113.22, 46.56) * mm, "end": v(113.11, 47.2) * mm});
            skArc(sketch, "E646", {"start": v(113.11, 47.2) * mm, "mid": v(113, 47.77) * mm, "end": v(112.85, 48.32) * mm});
            skArc(sketch, "E647", {"start": v(112.85, 48.32) * mm, "mid": v(112.72, 48.68) * mm, "end": v(112.54, 49.02) * mm});
            skArc(sketch, "E648", {"start": v(112.54, 49.02) * mm, "mid": v(111.92, 49.67) * mm, "end": v(111.1, 50.04) * mm});
            skArc(sketch, "E649", {"start": v(111.1, 50.04) * mm, "mid": v(107.56, 50.84) * mm, "end": v(104.01, 51.6) * mm});
            skArc(sketch, "E650", {"start": v(104.01, 51.6) * mm, "mid": v(100.5, 52.28) * mm, "end": v(96.98, 52.88) * mm});
            skArc(sketch, "E651", {"start": v(96.98, 52.88) * mm, "mid": v(94.56, 53.16) * mm, "end": v(92.12, 53.25) * mm});
            skArc(sketch, "E652", {"start": v(92.12, 53.25) * mm, "mid": v(91.27, 53.3) * mm, "end": v(90.42, 53.44) * mm});
            skArc(sketch, "E653", {"start": v(90.42, 53.44) * mm, "mid": v(89.9, 53.67) * mm, "end": v(89.5, 54.06) * mm});
            skArc(sketch, "E654", {"start": v(89.5, 54.06) * mm, "mid": v(89.37, 54.47) * mm, "end": v(89.5, 54.89) * mm});
            skArc(sketch, "E655", {"start": v(89.5, 54.89) * mm, "mid": v(89.89, 55.37) * mm, "end": v(90.37, 55.75) * mm});
            skArc(sketch, "E656", {"start": v(90.37, 55.75) * mm, "mid": v(90.87, 56.15) * mm, "end": v(91.27, 56.64) * mm});
            skArc(sketch, "E657", {"start": v(91.27, 56.64) * mm, "mid": v(91.37, 57.07) * mm, "end": v(91.2, 57.47) * mm});
            skArc(sketch, "E658", {"start": v(91.2, 57.47) * mm, "mid": v(90.72, 57.86) * mm, "end": v(90.14, 58.07) * mm});
            skArc(sketch, "E659", {"start": v(90.14, 58.07) * mm, "mid": v(89.17, 58.2) * mm, "end": v(88.2, 58.25) * mm});
            skArc(sketch, "E660", {"start": v(88.2, 58.25) * mm, "mid": v(86.39, 58.11) * mm, "end": v(84.62, 57.7) * mm});
            skArc(sketch, "E661", {"start": v(84.62, 57.7) * mm, "mid": v(82.53, 56.94) * mm, "end": v(80.51, 56) * mm});
            skArc(sketch, "E662", {"start": v(80.51, 56) * mm, "mid": v(78.48, 54.85) * mm, "end": v(76.56, 53.54) * mm});
            skArc(sketch, "E663", {"start": v(76.56, 53.54) * mm, "mid": v(74.91, 52.18) * mm, "end": v(73.42, 50.65) * mm});
            skArc(sketch, "E664", {"start": v(73.42, 50.65) * mm, "mid": v(72.37, 49.31) * mm, "end": v(71.47, 47.87) * mm});
            skArc(sketch, "E665", {"start": v(71.47, 47.87) * mm, "mid": v(70.87, 46.52) * mm, "end": v(70.5, 45.1) * mm});
            skArc(sketch, "E666", {"start": v(70.5, 45.1) * mm, "mid": v(70.45, 43.98) * mm, "end": v(70.67, 42.89) * mm});
            skArc(sketch, "E667", {"start": v(70.67, 42.89) * mm, "mid": v(71.13, 42.11) * mm, "end": v(71.87, 41.61) * mm});
            skArc(sketch, "E668", {"start": v(71.87, 41.61) * mm, "mid": v(72.17, 41.49) * mm, "end": v(72.45, 41.33) * mm});
            skArc(sketch, "E669", {"start": v(72.45, 41.33) * mm, "mid": v(72.7, 41.16) * mm, "end": v(72.93, 40.97) * mm});
            skArc(sketch, "E670", {"start": v(72.93, 40.97) * mm, "mid": v(73.11, 40.78) * mm, "end": v(73.27, 40.58) * mm});
            skArc(sketch, "E671", {"start": v(73.27, 40.58) * mm, "mid": v(73.35, 40.41) * mm, "end": v(73.37, 40.23) * mm});
            skArc(sketch, "E672", {"start": v(73.37, 40.23) * mm, "mid": v(73.2, 39.57) * mm, "end": v(72.75, 39.07) * mm});
            skArc(sketch, "E673", {"start": v(72.75, 39.07) * mm, "mid": v(71.07, 38.01) * mm, "end": v(69.36, 37) * mm});
            skArc(sketch, "E674", {"start": v(69.36, 37) * mm, "mid": v(67.04, 35.75) * mm, "end": v(64.67, 34.58) * mm});
            skArc(sketch, "E675", {"start": v(64.67, 34.58) * mm, "mid": v(61.6, 33.17) * mm, "end": v(58.5, 31.8) * mm});
            skLineSegment(sketch, "E676", {"start": v(58.5, 31.8) * mm, "end": v(50.18, 28.24) * mm});
            skLineSegment(sketch, "E677", {"start": v(50.18, 28.24) * mm, "end": v(53.78, 33) * mm});
            skArc(sketch, "E678", {"start": v(53.78, 33) * mm, "mid": v(57.51, 38.02) * mm, "end": v(61.14, 43.11) * mm});
            skArc(sketch, "E679", {"start": v(61.14, 43.11) * mm, "mid": v(62.92, 45.98) * mm, "end": v(64.38, 49.03) * mm});
            skArc(sketch, "E680", {"start": v(64.38, 49.03) * mm, "mid": v(64.75, 50.67) * mm, "end": v(64.55, 52.34) * mm});
            skArc(sketch, "E681", {"start": v(64.55, 52.34) * mm, "mid": v(63.8, 53.5) * mm, "end": v(62.52, 54.08) * mm});
            skArc(sketch, "E682", {"start": v(62.52, 54.08) * mm, "mid": v(61, 54.18) * mm, "end": v(59.46, 54.05) * mm});
            skArc(sketch, "E683", {"start": v(59.46, 54.05) * mm, "mid": v(57.92, 53.68) * mm, "end": v(56.44, 53.1) * mm});
            skArc(sketch, "E684", {"start": v(56.44, 53.1) * mm, "mid": v(54.46, 52.06) * mm, "end": v(52.57, 50.87) * mm});
            skArc(sketch, "E685", {"start": v(52.57, 50.87) * mm, "mid": v(49.39, 48.65) * mm, "end": v(46.24, 46.37) * mm});
            skArc(sketch, "E686", {"start": v(46.24, 46.37) * mm, "mid": v(40.17, 42.04) * mm, "end": v(33.96, 37.9) * mm});
            skArc(sketch, "E687", {"start": v(33.96, 37.9) * mm, "mid": v(29.75, 35.48) * mm, "end": v(25.3, 33.5) * mm});
            skArc(sketch, "E688", {"start": v(25.3, 33.5) * mm, "mid": v(22.7, 32.87) * mm, "end": v(20.03, 32.9) * mm});
            skArc(sketch, "E689", {"start": v(20.03, 32.9) * mm, "mid": v(18.37, 33.72) * mm, "end": v(17.57, 35.4) * mm});
            skArc(sketch, "E690", {"start": v(17.57, 35.4) * mm, "mid": v(17.82, 37.98) * mm, "end": v(19.1, 40.23) * mm});
            skArc(sketch, "E691", {"start": v(19.1, 40.23) * mm, "mid": v(21.98, 43.07) * mm, "end": v(25.19, 45.55) * mm});
            skArc(sketch, "E692", {"start": v(25.19, 45.55) * mm, "mid": v(29.67, 48.29) * mm, "end": v(34.4, 50.58) * mm});
            skArc(sketch, "E693", {"start": v(34.4, 50.58) * mm, "mid": v(40.02, 52.77) * mm, "end": v(45.76, 54.59) * mm});
            skArc(sketch, "E694", {"start": v(45.76, 54.59) * mm, "mid": v(47.56, 55.12) * mm, "end": v(49.33, 55.7) * mm});
            skArc(sketch, "E695", {"start": v(49.33, 55.7) * mm, "mid": v(51, 56.3) * mm, "end": v(52.66, 56.96) * mm});
            skArc(sketch, "E696", {"start": v(52.66, 56.96) * mm, "mid": v(54.04, 57.56) * mm, "end": v(55.4, 58.2) * mm});
            skArc(sketch, "E697", {"start": v(55.4, 58.2) * mm, "mid": v(56.1, 58.63) * mm, "end": v(56.73, 59.16) * mm});
            skArc(sketch, "E698", {"start": v(56.73, 59.16) * mm, "mid": v(57.35, 59.8) * mm, "end": v(57.94, 60.46) * mm});
            skArc(sketch, "E699", {"start": v(57.94, 60.46) * mm, "mid": v(58.15, 60.8) * mm, "end": v(58.25, 61.18) * mm});
            skArc(sketch, "E700", {"start": v(58.25, 61.18) * mm, "mid": v(58.22, 61.55) * mm, "end": v(58.06, 61.87) * mm});
            skArc(sketch, "E701", {"start": v(58.06, 61.87) * mm, "mid": v(57.6, 62.41) * mm, "end": v(57.13, 62.93) * mm});
            skArc(sketch, "E702", {"start": v(57.13, 62.93) * mm, "mid": v(55.21, 64.2) * mm, "end": v(52.95, 64.61) * mm});
            skArc(sketch, "E703", {"start": v(52.95, 64.61) * mm, "mid": v(48.8, 64.37) * mm, "end": v(44.68, 63.8) * mm});
            skArc(sketch, "E704", {"start": v(44.68, 63.8) * mm, "mid": v(39.76, 62.72) * mm, "end": v(34.94, 61.27) * mm});
            skArc(sketch, "E705", {"start": v(34.94, 61.27) * mm, "mid": v(30.06, 59.41) * mm, "end": v(25.32, 57.22) * mm});
            skArc(sketch, "E706", {"start": v(25.32, 57.22) * mm, "mid": v(22.43, 55.66) * mm, "end": v(19.63, 53.95) * mm});
            skArc(sketch, "E707", {"start": v(19.63, 53.95) * mm, "mid": v(16.98, 52.1) * mm, "end": v(14.43, 50.11) * mm});
            skArc(sketch, "E708", {"start": v(14.43, 50.11) * mm, "mid": v(12.3, 48.23) * mm, "end": v(10.3, 46.21) * mm});
            skArc(sketch, "E709", {"start": v(10.3, 46.21) * mm, "mid": v(9, 44.6) * mm, "end": v(7.96, 42.8) * mm});
            skArc(sketch, "E710", {"start": v(7.96, 42.8) * mm, "mid": v(6.45, 40.37) * mm, "end": v(4.41, 38.37) * mm});
            skArc(sketch, "E711", {"start": v(4.41, 38.37) * mm, "mid": v(0.84, 35.77) * mm, "end": v(-2.9, 33.42) * mm});
            skArc(sketch, "E712", {"start": v(-2.9, 33.42) * mm, "mid": v(-6.84, 31.3) * mm, "end": v(-10.92, 29.45) * mm});
            skArc(sketch, "E713", {"start": v(-10.92, 29.45) * mm, "mid": v(-13.9, 28.55) * mm, "end": v(-17, 28.25) * mm});
            skArc(sketch, "E714", {"start": v(-17, 28.25) * mm, "mid": v(-18.26, 28.39) * mm, "end": v(-19.46, 28.8) * mm});
            skArc(sketch, "E715", {"start": v(-19.46, 28.8) * mm, "mid": v(-20.8, 29.52) * mm, "end": v(-22.02, 30.41) * mm});
            skArc(sketch, "E716", {"start": v(-22.02, 30.41) * mm, "mid": v(-23.07, 31.41) * mm, "end": v(-23.98, 32.54) * mm});
            skArc(sketch, "E717", {"start": v(-23.98, 32.54) * mm, "mid": v(-24.46, 33.5) * mm, "end": v(-24.63, 34.57) * mm});
            skArc(sketch, "E718", {"start": v(-24.63, 34.57) * mm, "mid": v(-24.5, 35.3) * mm, "end": v(-24.12, 35.92) * mm});
            skArc(sketch, "E719", {"start": v(-24.12, 35.92) * mm, "mid": v(-23.39, 36.66) * mm, "end": v(-22.57, 37.29) * mm});
            skArc(sketch, "E720", {"start": v(-22.57, 37.29) * mm, "mid": v(-21.11, 38.2) * mm, "end": v(-19.6, 39) * mm});
            skArc(sketch, "E721", {"start": v(-19.6, 39) * mm, "mid": v(-16.75, 40.39) * mm, "end": v(-13.88, 41.74) * mm});
            skArc(sketch, "E722", {"start": v(-13.88, 41.74) * mm, "mid": v(-9.45, 43.93) * mm, "end": v(-5.14, 46.35) * mm});
            skArc(sketch, "E723", {"start": v(-5.14, 46.35) * mm, "mid": v(-1.67, 48.62) * mm, "end": v(1.6, 51.19) * mm});
            skArc(sketch, "E724", {"start": v(1.6, 51.19) * mm, "mid": v(3.92, 53.4) * mm, "end": v(6, 55.86) * mm});
            skArc(sketch, "E725", {"start": v(6, 55.86) * mm, "mid": v(7.02, 57.79) * mm, "end": v(7.37, 59.94) * mm});
            skArc(sketch, "E726", {"start": v(7.37, 59.94) * mm, "mid": v(7.35, 60.57) * mm, "end": v(7.26, 61.2) * mm});
            skArc(sketch, "E727", {"start": v(7.26, 61.2) * mm, "mid": v(7.12, 61.84) * mm, "end": v(6.93, 62.47) * mm});
            skArc(sketch, "E728", {"start": v(6.93, 62.47) * mm, "mid": v(6.71, 63.02) * mm, "end": v(6.45, 63.56) * mm});
            skArc(sketch, "E729", {"start": v(6.45, 63.56) * mm, "mid": v(6.2, 63.93) * mm, "end": v(5.87, 64.25) * mm});
            skArc(sketch, "E730", {"start": v(5.87, 64.25) * mm, "mid": v(4.7, 65) * mm, "end": v(3.37, 65.45) * mm});
            skArc(sketch, "E731", {"start": v(3.37, 65.45) * mm, "mid": v(1.43, 65.76) * mm, "end": v(-0.53, 65.88) * mm});
            skArc(sketch, "E732", {"start": v(-0.53, 65.88) * mm, "mid": v(-2.75, 65.82) * mm, "end": v(-4.95, 65.57) * mm});
            skArc(sketch, "E733", {"start": v(-4.95, 65.57) * mm, "mid": v(-7.07, 65.14) * mm, "end": v(-9.14, 64.5) * mm});
            skArc(sketch, "E734", {"start": v(-3.63, 56.75) * mm, "mid": v(-3.85, 55.57) * mm, "end": v(-4.49, 54.55) * mm});
            skArc(sketch, "E735", {"start": v(-4.49, 54.55) * mm, "mid": v(-6.26, 52.72) * mm, "end": v(-8.12, 50.99) * mm});
            skArc(sketch, "E736", {"start": v(-8.12, 50.99) * mm, "mid": v(-10.39, 49.1) * mm, "end": v(-12.75, 47.33) * mm});
            skArc(sketch, "E737", {"start": v(-12.75, 47.33) * mm, "mid": v(-15.15, 45.75) * mm, "end": v(-17.65, 44.32) * mm});
            skArc(sketch, "E738", {"start": v(-17.65, 44.32) * mm, "mid": v(-18.83, 43.7) * mm, "end": v(-20.03, 43.1) * mm});
            skArc(sketch, "E739", {"start": v(-20.03, 43.1) * mm, "mid": v(-21.07, 42.62) * mm, "end": v(-22.12, 42.17) * mm});
            skArc(sketch, "E740", {"start": v(-22.12, 42.17) * mm, "mid": v(-22.98, 41.81) * mm, "end": v(-23.86, 41.47) * mm});
            skArc(sketch, "E741", {"start": v(-23.86, 41.47) * mm, "mid": v(-24.08, 41.46) * mm, "end": v(-24.27, 41.56) * mm});
            skArc(sketch, "E742", {"start": v(-24.27, 41.56) * mm, "mid": v(-24.37, 41.73) * mm, "end": v(-24.38, 41.92) * mm});
            skArc(sketch, "E743", {"start": v(-24.38, 41.92) * mm, "mid": v(-24.3, 42.34) * mm, "end": v(-24.19, 42.75) * mm});
            skArc(sketch, "E744", {"start": v(-24.19, 42.75) * mm, "mid": v(-24.02, 43.27) * mm, "end": v(-23.82, 43.78) * mm});
            skArc(sketch, "E745", {"start": v(-23.82, 43.78) * mm, "mid": v(-23.56, 44.35) * mm, "end": v(-23.28, 44.9) * mm});
            skArc(sketch, "E746", {"start": v(-23.28, 44.9) * mm, "mid": v(-21.38, 47.86) * mm, "end": v(-18.99, 50.43) * mm});
            skArc(sketch, "E747", {"start": v(-18.99, 50.43) * mm, "mid": v(-15.6, 53.19) * mm, "end": v(-11.97, 55.62) * mm});
            skArc(sketch, "E748", {"start": v(-11.97, 55.62) * mm, "mid": v(-8.96, 57.18) * mm, "end": v(-5.77, 58.35) * mm});
            skArc(sketch, "E749", {"start": v(-5.77, 58.35) * mm, "mid": v(-4.3, 58.09) * mm, "end": v(-3.63, 56.75) * mm});
            skArc(sketch, "E750", {"start": v(143.5, 25.67) * mm, "mid": v(142.3, 24.54) * mm, "end": v(141.13, 23.36) * mm});
            skArc(sketch, "E751", {"start": v(141.13, 23.36) * mm, "mid": v(140.2, 22.3) * mm, "end": v(139.34, 21.2) * mm});
            skArc(sketch, "E752", {"start": v(139.34, 21.2) * mm, "mid": v(138.65, 20.16) * mm, "end": v(138.04, 19.08) * mm});
            skArc(sketch, "E753", {"start": v(138.04, 19.08) * mm, "mid": v(137.57, 18.02) * mm, "end": v(137.19, 16.92) * mm});
            skArc(sketch, "E754", {"start": v(137.19, 16.92) * mm, "mid": v(136.93, 16.1) * mm, "end": v(136.65, 15.27) * mm});
            skArc(sketch, "E755", {"start": v(136.65, 15.27) * mm, "mid": v(136.35, 14.51) * mm, "end": v(136.02, 13.76) * mm});
            skArc(sketch, "E756", {"start": v(136.02, 13.76) * mm, "mid": v(135.72, 13.15) * mm, "end": v(135.4, 12.55) * mm});
            skArc(sketch, "E757", {"start": v(135.4, 12.55) * mm, "mid": v(135.2, 12.25) * mm, "end": v(134.92, 12.02) * mm});
            skArc(sketch, "E758", {"start": v(134.92, 12.02) * mm, "mid": v(134.04, 11.56) * mm, "end": v(133.07, 11.36) * mm});
            skArc(sketch, "E759", {"start": v(133.07, 11.36) * mm, "mid": v(131.22, 11.29) * mm, "end": v(129.37, 11.3) * mm});
            skArc(sketch, "E760", {"start": v(129.37, 11.3) * mm, "mid": v(127.46, 11.42) * mm, "end": v(125.56, 11.64) * mm});
            skArc(sketch, "E761", {"start": v(125.56, 11.64) * mm, "mid": v(124.21, 11.93) * mm, "end": v(122.92, 12.41) * mm});
            skArc(sketch, "E762", {"start": v(122.92, 12.41) * mm, "mid": v(121.97, 12.98) * mm, "end": v(121.16, 13.74) * mm});
            skArc(sketch, "E763", {"start": v(121.16, 13.74) * mm, "mid": v(120.68, 14.55) * mm, "end": v(120.5, 15.48) * mm});
            skArc(sketch, "E764", {"start": v(120.5, 15.48) * mm, "mid": v(120.62, 16.68) * mm, "end": v(121, 17.84) * mm});
            skArc(sketch, "E765", {"start": v(121, 17.84) * mm, "mid": v(121.85, 19.51) * mm, "end": v(122.8, 21.13) * mm});
            skArc(sketch, "E766", {"start": v(122.8, 21.13) * mm, "mid": v(124.3, 23.05) * mm, "end": v(126.15, 24.62) * mm});
            skArc(sketch, "E767", {"start": v(126.15, 24.62) * mm, "mid": v(128.68, 26.16) * mm, "end": v(131.36, 27.39) * mm});
            skArc(sketch, "E768", {"start": v(131.36, 27.39) * mm, "mid": v(134.64, 28.5) * mm, "end": v(138.01, 29.28) * mm});
            skArc(sketch, "E769", {"start": v(138.01, 29.28) * mm, "mid": v(141.86, 29.84) * mm, "end": v(145.73, 30.13) * mm});
            skArc(sketch, "E770", {"start": v(145.73, 30.13) * mm, "mid": v(146.51, 30.13) * mm, "end": v(147.29, 30.07) * mm});
            skArc(sketch, "E771", {"start": v(147.29, 30.07) * mm, "mid": v(147.52, 29.9) * mm, "end": v(147.53, 29.62) * mm});
            skArc(sketch, "E772", {"start": v(147.53, 29.62) * mm, "mid": v(147.23, 29.14) * mm, "end": v(146.84, 28.72) * mm});
            skArc(sketch, "E773", {"start": v(146.84, 28.72) * mm, "mid": v(145.18, 27.2) * mm, "end": v(143.5, 25.67) * mm});
            skArc(sketch, "E774", {"start": v(-145.76, 22.22) * mm, "mid": v(-146.17, 20.04) * mm, "end": v(-146.39, 17.84) * mm});
            skArc(sketch, "E775", {"start": v(-146.39, 17.84) * mm, "mid": v(-146.42, 15.64) * mm, "end": v(-146.26, 13.44) * mm});
            skArc(sketch, "E776", {"start": v(-146.26, 13.44) * mm, "mid": v(-145.95, 11.52) * mm, "end": v(-145.45, 9.65) * mm});
            skArc(sketch, "E777", {"start": v(-145.45, 9.65) * mm, "mid": v(-144.87, 8.3) * mm, "end": v(-144.01, 7.13) * mm});
            skArc(sketch, "E778", {"start": v(-144.01, 7.13) * mm, "mid": v(-143.5, 6.48) * mm, "end": v(-143.06, 5.77) * mm});
            skArc(sketch, "E779", {"start": v(-143.06, 5.77) * mm, "mid": v(-142.92, 5.28) * mm, "end": v(-143.02, 4.77) * mm});
            skArc(sketch, "E780", {"start": v(-143.02, 4.77) * mm, "mid": v(-143.37, 4.13) * mm, "end": v(-143.84, 3.57) * mm});
            skArc(sketch, "E781", {"start": v(-143.84, 3.57) * mm, "mid": v(-145.33, 2.11) * mm, "end": v(-146.84, 0.67) * mm});
            skArc(sketch, "E782", {"start": v(-146.84, 0.67) * mm, "mid": v(-148.62, -0.88) * mm, "end": v(-150.54, -2.26) * mm});
            skArc(sketch, "E783", {"start": v(-150.54, -2.26) * mm, "mid": v(-152.19, -3.15) * mm, "end": v(-153.97, -3.74) * mm});
            skArc(sketch, "E784", {"start": v(-153.97, -3.74) * mm, "mid": v(-155.26, -3.85) * mm, "end": v(-156.53, -3.58) * mm});
            skArc(sketch, "E785", {"start": v(-156.53, -3.58) * mm, "mid": v(-157.46, -2.96) * mm, "end": v(-158, -2) * mm});
            skArc(sketch, "E786", {"start": v(-158, -2) * mm, "mid": v(-158.56, 0.06) * mm, "end": v(-159, 2.13) * mm});
            skArc(sketch, "E787", {"start": v(-159, 2.13) * mm, "mid": v(-159.23, 3.73) * mm, "end": v(-159.28, 5.34) * mm});
            skArc(sketch, "E788", {"start": v(-159.28, 5.34) * mm, "mid": v(-159.16, 6.76) * mm, "end": v(-158.86, 8.16) * mm});
            skArc(sketch, "E789", {"start": v(-158.86, 8.16) * mm, "mid": v(-158.37, 9.63) * mm, "end": v(-157.73, 11.05) * mm});
            skArc(sketch, "E790", {"start": v(-157.73, 11.05) * mm, "mid": v(-156.62, 13.02) * mm, "end": v(-155.36, 14.9) * mm});
            skArc(sketch, "E791", {"start": v(-155.36, 14.9) * mm, "mid": v(-153.14, 17.89) * mm, "end": v(-150.86, 20.83) * mm});
            skArc(sketch, "E792", {"start": v(-150.86, 20.83) * mm, "mid": v(-148.4, 23.92) * mm, "end": v(-145.92, 27) * mm});
            skArc(sketch, "E793", {"start": v(-145.92, 27) * mm, "mid": v(-145.51, 27.2) * mm, "end": v(-145.09, 27.05) * mm});
            skArc(sketch, "E794", {"start": v(-145.09, 27.05) * mm, "mid": v(-145, 26.91) * mm, "end": v(-144.98, 26.75) * mm});
            skArc(sketch, "E795", {"start": v(-144.98, 26.75) * mm, "mid": v(-145.06, 26.12) * mm, "end": v(-145.14, 25.49) * mm});
            skArc(sketch, "E796", {"start": v(-145.14, 25.49) * mm, "mid": v(-145.26, 24.72) * mm, "end": v(-145.4, 23.96) * mm});
            skArc(sketch, "E797", {"start": v(-145.4, 23.96) * mm, "mid": v(-145.57, 23.1) * mm, "end": v(-145.76, 22.22) * mm});
            skArc(sketch, "E798", {"start": v(-32.63, 1.12) * mm, "mid": v(-36.03, -1.05) * mm, "end": v(-39.37, -3.32) * mm});
            skArc(sketch, "E799", {"start": v(-39.37, -3.32) * mm, "mid": v(-42.8, -5.79) * mm, "end": v(-46.18, -8.34) * mm});
            skArc(sketch, "E800", {"start": v(-46.18, -8.34) * mm, "mid": v(-49.74, -11.18) * mm, "end": v(-53.24, -14.1) * mm});
            skArc(sketch, "E801", {"start": v(-53.24, -14.1) * mm, "mid": v(-57.02, -17.4) * mm, "end": v(-60.75, -20.75) * mm});
            skArc(sketch, "E802", {"start": v(-60.75, -20.75) * mm, "mid": v(-63.4, -23.16) * mm, "end": v(-66.1, -25.55) * mm});
            skArc(sketch, "E803", {"start": v(-66.1, -25.55) * mm, "mid": v(-67.4, -26.6) * mm, "end": v(-68.8, -27.54) * mm});
            skArc(sketch, "E804", {"start": v(-68.8, -27.54) * mm, "mid": v(-69.89, -28.08) * mm, "end": v(-71.04, -28.43) * mm});
            skArc(sketch, "E805", {"start": v(-71.04, -28.43) * mm, "mid": v(-72.41, -28.65) * mm, "end": v(-73.8, -28.72) * mm});
            skArc(sketch, "E806", {"start": v(-73.8, -28.72) * mm, "mid": v(-75.2, -28.7) * mm, "end": v(-76.6, -28.67) * mm});
            skArc(sketch, "E807", {"start": v(-76.6, -28.67) * mm, "mid": v(-76.92, -28.61) * mm, "end": v(-77.22, -28.46) * mm});
            skArc(sketch, "E808", {"start": v(-77.22, -28.46) * mm, "mid": v(-77.33, -28.28) * mm, "end": v(-77.25, -28.08) * mm});
            skArc(sketch, "E809", {"start": v(-77.25, -28.08) * mm, "mid": v(-76.7, -27.58) * mm, "end": v(-76.13, -27.1) * mm});
            skArc(sketch, "E810", {"start": v(-76.13, -27.1) * mm, "mid": v(-75.48, -26.58) * mm, "end": v(-74.83, -26.05) * mm});
            skArc(sketch, "E811", {"start": v(-74.83, -26.05) * mm, "mid": v(-74.78, -25.94) * mm, "end": v(-74.83, -25.83) * mm});
            skArc(sketch, "E812", {"start": v(-74.83, -25.83) * mm, "mid": v(-74.97, -25.75) * mm, "end": v(-75.12, -25.75) * mm});
            skArc(sketch, "E813", {"start": v(-75.12, -25.75) * mm, "mid": v(-76.12, -25.97) * mm, "end": v(-77.13, -26.2) * mm});
            skArc(sketch, "E814", {"start": v(-77.13, -26.2) * mm, "mid": v(-78.63, -26.61) * mm, "end": v(-80.1, -27.16) * mm});
            skArc(sketch, "E815", {"start": v(-80.1, -27.16) * mm, "mid": v(-81.4, -27.81) * mm, "end": v(-82.64, -28.6) * mm});
            skArc(sketch, "E816", {"start": v(-82.64, -28.6) * mm, "mid": v(-83.78, -29.52) * mm, "end": v(-84.82, -30.56) * mm});
            skArc(sketch, "E817", {"start": v(-84.82, -30.56) * mm, "mid": v(-85.8, -31.76) * mm, "end": v(-86.67, -33.05) * mm});
            skArc(sketch, "E818", {"start": v(-86.67, -33.05) * mm, "mid": v(-87.05, -33.69) * mm, "end": v(-87.42, -34.32) * mm});
            skArc(sketch, "E819", {"start": v(-87.42, -34.32) * mm, "mid": v(-87.74, -34.9) * mm, "end": v(-88.05, -35.5) * mm});
            skArc(sketch, "E820", {"start": v(-88.05, -35.5) * mm, "mid": v(-88.3, -36) * mm, "end": v(-88.53, -36.5) * mm});
            skArc(sketch, "E821", {"start": v(-88.53, -36.5) * mm, "mid": v(-88.6, -36.69) * mm, "end": v(-88.62, -36.9) * mm});
            skArc(sketch, "E822", {"start": v(-88.62, -36.9) * mm, "mid": v(-88.57, -37.07) * mm, "end": v(-88.43, -37.18) * mm});
            skArc(sketch, "E823", {"start": v(-88.43, -37.18) * mm, "mid": v(-87.87, -37.4) * mm, "end": v(-87.3, -37.6) * mm});
            skArc(sketch, "E824", {"start": v(-87.3, -37.6) * mm, "mid": v(-86.58, -37.82) * mm, "end": v(-85.85, -38.01) * mm});
            skArc(sketch, "E825", {"start": v(-85.85, -38.01) * mm, "mid": v(-85, -38.21) * mm, "end": v(-84.13, -38.4) * mm});
            skLineSegment(sketch, "E826", {"start": v(-84.13, -38.4) * mm, "end": v(-79.64, -39.25) * mm});
            skLineSegment(sketch, "E827", {"start": v(-79.64, -39.25) * mm, "end": v(-83.7, -44) * mm});
            skArc(sketch, "E828", {"start": v(-83.7, -44) * mm, "mid": v(-84.63, -45.03) * mm, "end": v(-85.58, -46.02) * mm});
            skArc(sketch, "E829", {"start": v(-85.58, -46.02) * mm, "mid": v(-86.42, -46.8) * mm, "end": v(-87.3, -47.51) * mm});
            skArc(sketch, "E830", {"start": v(-87.3, -47.51) * mm, "mid": v(-88.04, -48.02) * mm, "end": v(-88.8, -48.46) * mm});
            skArc(sketch, "E831", {"start": v(-88.8, -48.46) * mm, "mid": v(-89.4, -48.67) * mm, "end": v(-90.01, -48.75) * mm});
            skArc(sketch, "E832", {"start": v(-90.01, -48.75) * mm, "mid": v(-91.15, -48.92) * mm, "end": v(-92.19, -49.4) * mm});
            skArc(sketch, "E833", {"start": v(-92.19, -49.4) * mm, "mid": v(-93.75, -50.51) * mm, "end": v(-95.23, -51.73) * mm});
            skArc(sketch, "E834", {"start": v(-95.23, -51.73) * mm, "mid": v(-96.82, -53.24) * mm, "end": v(-98.3, -54.85) * mm});
            skArc(sketch, "E835", {"start": v(-98.3, -54.85) * mm, "mid": v(-99.6, -56.5) * mm, "end": v(-100.78, -58.25) * mm});
            skArc(sketch, "E836", {"start": v(-100.78, -58.25) * mm, "mid": v(-101.52, -59.52) * mm, "end": v(-102.19, -60.84) * mm});
            skArc(sketch, "E837", {"start": v(-102.19, -60.84) * mm, "mid": v(-102.46, -61.63) * mm, "end": v(-102.52, -62.47) * mm});
            skArc(sketch, "E838", {"start": v(-102.52, -62.47) * mm, "mid": v(-102.35, -63) * mm, "end": v(-101.94, -63.4) * mm});
            skArc(sketch, "E839", {"start": v(-101.94, -63.4) * mm, "mid": v(-101.26, -63.66) * mm, "end": v(-100.53, -63.75) * mm});
            skArc(sketch, "E840", {"start": v(-100.53, -63.75) * mm, "mid": v(-99.77, -63.62) * mm, "end": v(-99.1, -63.26) * mm});
            skArc(sketch, "E841", {"start": v(-99.1, -63.26) * mm, "mid": v(-97.36, -61.9) * mm, "end": v(-95.66, -60.49) * mm});
            skArc(sketch, "E842", {"start": v(-95.66, -60.49) * mm, "mid": v(-93.44, -58.56) * mm, "end": v(-91.27, -56.58) * mm});
            skArc(sketch, "E843", {"start": v(-91.27, -56.58) * mm, "mid": v(-88.47, -53.93) * mm, "end": v(-85.7, -51.25) * mm});
            skLineSegment(sketch, "E844", {"start": v(-85.7, -51.25) * mm, "end": v(-72.97, -38.75) * mm});
            skLineSegment(sketch, "E845", {"start": v(-72.97, -38.75) * mm, "end": v(-63.3, -38.75) * mm});
            skArc(sketch, "E846", {"start": v(-63.3, -38.75) * mm, "mid": v(-61.44, -38.76) * mm, "end": v(-59.59, -38.79) * mm});
            skArc(sketch, "E847", {"start": v(-59.59, -38.79) * mm, "mid": v(-58.03, -38.83) * mm, "end": v(-56.47, -38.9) * mm});
            skArc(sketch, "E848", {"start": v(-56.47, -38.9) * mm, "mid": v(-55.15, -38.98) * mm, "end": v(-53.82, -39.06) * mm});
            skArc(sketch, "E849", {"start": v(-53.82, -39.06) * mm, "mid": v(-53.68, -39.13) * mm, "end": v(-53.63, -39.27) * mm});
            skArc(sketch, "E850", {"start": v(-53.63, -39.27) * mm, "mid": v(-53.65, -39.47) * mm, "end": v(-53.7, -39.65) * mm});
            skArc(sketch, "E851", {"start": v(-53.7, -39.65) * mm, "mid": v(-54.18, -40.67) * mm, "end": v(-54.65, -41.69) * mm});
            skArc(sketch, "E852", {"start": v(-54.65, -41.69) * mm, "mid": v(-55.21, -42.87) * mm, "end": v(-55.78, -44.05) * mm});
            skArc(sketch, "E853", {"start": v(-55.78, -44.05) * mm, "mid": v(-56.45, -45.4) * mm, "end": v(-57.13, -46.75) * mm});
            skArc(sketch, "E854", {"start": v(-57.13, -46.75) * mm, "mid": v(-58.4, -49.35) * mm, "end": v(-59.59, -52) * mm});
            skArc(sketch, "E855", {"start": v(-59.59, -52) * mm, "mid": v(-60.12, -53.49) * mm, "end": v(-60.43, -55.05) * mm});
            skArc(sketch, "E856", {"start": v(-60.43, -55.05) * mm, "mid": v(-60.41, -56.17) * mm, "end": v(-60.1, -57.24) * mm});
            skArc(sketch, "E857", {"start": v(-60.1, -57.24) * mm, "mid": v(-59.48, -58.3) * mm, "end": v(-58.67, -59.21) * mm});
            skArc(sketch, "E858", {"start": v(-58.67, -59.21) * mm, "mid": v(-57.65, -59.9) * mm, "end": v(-56.5, -60.31) * mm});
            skArc(sketch, "E859", {"start": v(-56.5, -60.31) * mm, "mid": v(-55.25, -60.41) * mm, "end": v(-54.01, -60.2) * mm});
            skArc(sketch, "E860", {"start": v(-54.01, -60.2) * mm, "mid": v(-52.32, -59.55) * mm, "end": v(-50.73, -58.68) * mm});
            skArc(sketch, "E861", {"start": v(-50.73, -58.68) * mm, "mid": v(-48.21, -57.01) * mm, "end": v(-45.75, -55.26) * mm});
            skArc(sketch, "E862", {"start": v(-45.75, -55.26) * mm, "mid": v(-43.41, -53.5) * mm, "end": v(-41.1, -51.7) * mm});
            skArc(sketch, "E863", {"start": v(-41.1, -51.7) * mm, "mid": v(-40.36, -50.91) * mm, "end": v(-39.85, -49.96) * mm});
            skArc(sketch, "E864", {"start": v(-39.85, -49.96) * mm, "mid": v(-39.95, -49.49) * mm, "end": v(-40.42, -49.38) * mm});
            skArc(sketch, "E865", {"start": v(-40.42, -49.38) * mm, "mid": v(-42.3, -50.13) * mm, "end": v(-44.13, -50.96) * mm});
            skArc(sketch, "E866", {"start": v(-44.13, -50.96) * mm, "mid": v(-46.14, -51.85) * mm, "end": v(-48.21, -52.6) * mm});
            skArc(sketch, "E867", {"start": v(-48.21, -52.6) * mm, "mid": v(-49.12, -52.59) * mm, "end": v(-49.82, -52) * mm});
            skArc(sketch, "E868", {"start": v(-49.82, -52) * mm, "mid": v(-50.14, -50.98) * mm, "end": v(-49.98, -49.92) * mm});
            skArc(sketch, "E869", {"start": v(-49.98, -49.92) * mm, "mid": v(-48.9, -47.41) * mm, "end": v(-47.73, -44.96) * mm});
            skArc(sketch, "E870", {"start": v(-47.73, -44.96) * mm, "mid": v(-46.87, -43.3) * mm, "end": v(-45.96, -41.68) * mm});
            skArc(sketch, "E871", {"start": v(-45.96, -41.68) * mm, "mid": v(-45.35, -40.75) * mm, "end": v(-44.64, -39.9) * mm});
            skArc(sketch, "E872", {"start": v(-44.64, -39.9) * mm, "mid": v(-44, -39.33) * mm, "end": v(-43.25, -38.88) * mm});
            skArc(sketch, "E873", {"start": v(-43.25, -38.88) * mm, "mid": v(-42.35, -38.51) * mm, "end": v(-41.4, -38.26) * mm});
            skArc(sketch, "E874", {"start": v(-41.4, -38.26) * mm, "mid": v(-40.72, -38.12) * mm, "end": v(-40.03, -37.97) * mm});
            skArc(sketch, "E875", {"start": v(-40.03, -37.97) * mm, "mid": v(-39.32, -37.82) * mm, "end": v(-38.61, -37.66) * mm});
            skArc(sketch, "E876", {"start": v(-38.61, -37.66) * mm, "mid": v(-37.98, -37.52) * mm, "end": v(-37.35, -37.37) * mm});
            skArc(sketch, "E877", {"start": v(-37.35, -37.37) * mm, "mid": v(-36.93, -37.26) * mm, "end": v(-36.5, -37.15) * mm});
            skArc(sketch, "E878", {"start": v(-36.5, -37.15) * mm, "mid": v(-35.78, -37.14) * mm, "end": v(-35.15, -37.5) * mm});
            skArc(sketch, "E879", {"start": v(-35.15, -37.5) * mm, "mid": v(-34.48, -38.33) * mm, "end": v(-33.96, -39.26) * mm});
            skArc(sketch, "E880", {"start": v(-33.96, -39.26) * mm, "mid": v(-33.38, -40.76) * mm, "end": v(-32.97, -42.33) * mm});
            skArc(sketch, "E881", {"start": v(-32.97, -42.33) * mm, "mid": v(-32.58, -44.49) * mm, "end": v(-32.28, -46.66) * mm});
            skArc(sketch, "E882", {"start": v(-32.28, -46.66) * mm, "mid": v(-31.98, -48.46) * mm, "end": v(-31.49, -50.21) * mm});
            skArc(sketch, "E883", {"start": v(-31.49, -50.21) * mm, "mid": v(-30.83, -51.81) * mm, "end": v(-29.99, -53.32) * mm});
            skArc(sketch, "E884", {"start": v(-29.99, -53.32) * mm, "mid": v(-29.1, -54.52) * mm, "end": v(-28.05, -55.57) * mm});
            skArc(sketch, "E885", {"start": v(-28.05, -55.57) * mm, "mid": v(-27.06, -56.21) * mm, "end": v(-25.93, -56.55) * mm});
            skArc(sketch, "E886", {"start": v(-25.93, -56.55) * mm, "mid": v(-24.97, -56.53) * mm, "end": v(-24.06, -56.2) * mm});
            skArc(sketch, "E887", {"start": v(-24.06, -56.2) * mm, "mid": v(-22.8, -55.4) * mm, "end": v(-21.6, -54.48) * mm});
            skArc(sketch, "E888", {"start": v(-21.6, -54.48) * mm, "mid": v(-19.94, -52.97) * mm, "end": v(-18.38, -51.36) * mm});
            skArc(sketch, "E889", {"start": v(-18.38, -51.36) * mm, "mid": v(-16.1, -48.83) * mm, "end": v(-13.88, -46.25) * mm});
            skLineSegment(sketch, "E890", {"start": v(-13.88, -46.25) * mm, "end": v(-9.64, -41.25) * mm});
            skLineSegment(sketch, "E891", {"start": v(-9.64, -41.25) * mm, "end": v(-11.7, -46.03) * mm});
            skArc(sketch, "E892", {"start": v(-11.7, -46.03) * mm, "mid": v(-12.1, -47.05) * mm, "end": v(-12.46, -48.1) * mm});
            skArc(sketch, "E893", {"start": v(-12.46, -48.1) * mm, "mid": v(-12.78, -49.22) * mm, "end": v(-13.05, -50.35) * mm});
            skArc(sketch, "E894", {"start": v(-13.05, -50.35) * mm, "mid": v(-13.26, -51.4) * mm, "end": v(-13.41, -52.46) * mm});
            skArc(sketch, "E895", {"start": v(-13.41, -52.46) * mm, "mid": v(-13.47, -53.25) * mm, "end": v(-13.44, -54.03) * mm});
            skArc(sketch, "E896", {"start": v(-13.44, -54.03) * mm, "mid": v(-13.32, -54.9) * mm, "end": v(-13.16, -55.74) * mm});
            skArc(sketch, "E897", {"start": v(-13.16, -55.74) * mm, "mid": v(-12.97, -56.25) * mm, "end": v(-12.66, -56.7) * mm});
            skArc(sketch, "E898", {"start": v(-12.66, -56.7) * mm, "mid": v(-12.28, -57.04) * mm, "end": v(-11.81, -57.26) * mm});
            skArc(sketch, "E899", {"start": v(-11.81, -57.26) * mm, "mid": v(-11.1, -57.45) * mm, "end": v(-10.35, -57.57) * mm});
            skArc(sketch, "E900", {"start": v(-10.35, -57.57) * mm, "mid": v(-9.05, -57.58) * mm, "end": v(-7.76, -57.32) * mm});
            skArc(sketch, "E901", {"start": v(-7.76, -57.32) * mm, "mid": v(-6.2, -56.75) * mm, "end": v(-4.7, -56.02) * mm});
            skArc(sketch, "E902", {"start": v(-4.7, -56.02) * mm, "mid": v(-3.02, -54.98) * mm, "end": v(-1.43, -53.8) * mm});
            skArc(sketch, "E903", {"start": v(-1.43, -53.8) * mm, "mid": v(0.24, -52.36) * mm, "end": v(1.81, -50.82) * mm});
            skArc(sketch, "E904", {"start": v(1.81, -50.82) * mm, "mid": v(3, -49.6) * mm, "end": v(4.23, -48.42) * mm});
            skArc(sketch, "E905", {"start": v(4.23, -48.42) * mm, "mid": v(4.74, -48.08) * mm, "end": v(5.34, -47.94) * mm});
            skArc(sketch, "E906", {"start": v(5.34, -47.94) * mm, "mid": v(5.8, -48.06) * mm, "end": v(6.1, -48.44) * mm});
            skArc(sketch, "E907", {"start": v(6.1, -48.44) * mm, "mid": v(6.43, -49.47) * mm, "end": v(6.68, -50.52) * mm});
            skArc(sketch, "E908", {"start": v(6.68, -50.52) * mm, "mid": v(7.03, -51.8) * mm, "end": v(7.55, -53) * mm});
            skArc(sketch, "E909", {"start": v(7.55, -53) * mm, "mid": v(8.35, -54.43) * mm, "end": v(9.25, -55.8) * mm});
            skArc(sketch, "E910", {"start": v(9.25, -55.8) * mm, "mid": v(10.17, -57) * mm, "end": v(11.17, -58.15) * mm});
            skArc(sketch, "E911", {"start": v(11.17, -58.15) * mm, "mid": v(11.8, -58.6) * mm, "end": v(12.55, -58.75) * mm});
            skArc(sketch, "E912", {"start": v(12.55, -58.75) * mm, "mid": v(12.9, -58.69) * mm, "end": v(13.2, -58.52) * mm});
            skArc(sketch, "E913", {"start": v(13.2, -58.52) * mm, "mid": v(14.3, -57.61) * mm, "end": v(15.4, -56.7) * mm});
            skArc(sketch, "E914", {"start": v(15.4, -56.7) * mm, "mid": v(16.7, -55.58) * mm, "end": v(17.96, -54.44) * mm});
            skArc(sketch, "E915", {"start": v(17.96, -54.44) * mm, "mid": v(19.38, -53.1) * mm, "end": v(20.8, -51.76) * mm});
            skLineSegment(sketch, "E916", {"start": v(20.8, -51.76) * mm, "end": v(28, -44.77) * mm});
            skLineSegment(sketch, "E917", {"start": v(28, -44.77) * mm, "end": v(27.58, -50.62) * mm});
            skArc(sketch, "E918", {"start": v(27.58, -50.62) * mm, "mid": v(27.54, -54.24) * mm, "end": v(27.93, -57.83) * mm});
            skArc(sketch, "E919", {"start": v(27.93, -57.83) * mm, "mid": v(28.84, -59.6) * mm, "end": v(30.6, -60.55) * mm});
            skArc(sketch, "E920", {"start": v(30.6, -60.55) * mm, "mid": v(32.97, -60.52) * mm, "end": v(35.13, -59.52) * mm});
            skArc(sketch, "E921", {"start": v(35.13, -59.52) * mm, "mid": v(38.73, -56.64) * mm, "end": v(42.12, -53.5) * mm});
            skArc(sketch, "E922", {"start": v(42.12, -53.5) * mm, "mid": v(43.88, -51.78) * mm, "end": v(45.66, -50.07) * mm});
            skArc(sketch, "E923", {"start": v(45.66, -50.07) * mm, "mid": v(46.42, -49.4) * mm, "end": v(47.25, -48.82) * mm});
            skArc(sketch, "E924", {"start": v(47.25, -48.82) * mm, "mid": v(47.63, -48.72) * mm, "end": v(48, -48.85) * mm});
            skArc(sketch, "E925", {"start": v(48, -48.85) * mm, "mid": v(48.27, -49.17) * mm, "end": v(48.37, -49.58) * mm});
            skArc(sketch, "E926", {"start": v(48.37, -49.58) * mm, "mid": v(48.48, -50.93) * mm, "end": v(48.8, -52.25) * mm});
            skArc(sketch, "E927", {"start": v(48.8, -52.25) * mm, "mid": v(49.37, -53.67) * mm, "end": v(50.08, -55.01) * mm});
            skArc(sketch, "E928", {"start": v(50.08, -55.01) * mm, "mid": v(50.9, -56.18) * mm, "end": v(51.84, -57.24) * mm});
            skArc(sketch, "E929", {"start": v(51.84, -57.24) * mm, "mid": v(52.69, -57.9) * mm, "end": v(53.68, -58.29) * mm});
            skArc(sketch, "E930", {"start": v(53.68, -58.29) * mm, "mid": v(55, -58.48) * mm, "end": v(56.35, -58.4) * mm});
            skArc(sketch, "E931", {"start": v(56.35, -58.4) * mm, "mid": v(57.82, -58.03) * mm, "end": v(59.24, -57.47) * mm});
            skArc(sketch, "E932", {"start": v(59.24, -57.47) * mm, "mid": v(60.93, -56.54) * mm, "end": v(62.52, -55.43) * mm});
            skArc(sketch, "E933", {"start": v(62.52, -55.43) * mm, "mid": v(64.5, -53.82) * mm, "end": v(66.4, -52.13) * mm});
            skArc(sketch, "E934", {"start": v(66.4, -52.13) * mm, "mid": v(67.58, -51.04) * mm, "end": v(68.78, -49.98) * mm});
            skArc(sketch, "E935", {"start": v(68.78, -49.98) * mm, "mid": v(69.48, -49.43) * mm, "end": v(70.24, -48.94) * mm});
            skArc(sketch, "E936", {"start": v(70.24, -48.94) * mm, "mid": v(70.6, -48.8) * mm, "end": v(71, -48.78) * mm});
            skArc(sketch, "E937", {"start": v(71, -48.78) * mm, "mid": v(71.27, -48.93) * mm, "end": v(71.37, -49.2) * mm});
            skArc(sketch, "E938", {"start": v(71.37, -49.2) * mm, "mid": v(71.5, -50.38) * mm, "end": v(71.85, -51.5) * mm});
            skArc(sketch, "E939", {"start": v(71.85, -51.5) * mm, "mid": v(72.52, -52.84) * mm, "end": v(73.33, -54.11) * mm});
            skArc(sketch, "E940", {"start": v(73.33, -54.11) * mm, "mid": v(74.27, -55.31) * mm, "end": v(75.33, -56.41) * mm});
            skArc(sketch, "E941", {"start": v(75.33, -56.41) * mm, "mid": v(76.3, -57.18) * mm, "end": v(77.41, -57.76) * mm});
            skArc(sketch, "E942", {"start": v(77.41, -57.76) * mm, "mid": v(78.76, -58.2) * mm, "end": v(80.16, -58.4) * mm});
            skArc(sketch, "E943", {"start": v(80.16, -58.4) * mm, "mid": v(81.53, -58.34) * mm, "end": v(82.86, -58.04) * mm});
            skArc(sketch, "E944", {"start": v(82.86, -58.04) * mm, "mid": v(84.29, -57.45) * mm, "end": v(85.6, -56.65) * mm});
            skArc(sketch, "E945", {"start": v(85.6, -56.65) * mm, "mid": v(87.08, -55.47) * mm, "end": v(88.45, -54.17) * mm});
            skArc(sketch, "E946", {"start": v(88.45, -54.17) * mm, "mid": v(89.23, -53.41) * mm, "end": v(90.04, -52.7) * mm});
            skArc(sketch, "E947", {"start": v(90.04, -52.7) * mm, "mid": v(90.8, -52.13) * mm, "end": v(91.6, -51.63) * mm});
            skArc(sketch, "E948", {"start": v(91.6, -51.63) * mm, "mid": v(92.32, -51.26) * mm, "end": v(93.08, -50.97) * mm});
            skArc(sketch, "E949", {"start": v(93.08, -50.97) * mm, "mid": v(93.75, -50.8) * mm, "end": v(94.44, -50.75) * mm});
            skArc(sketch, "E950", {"start": v(94.44, -50.75) * mm, "mid": v(95.67, -50.62) * mm, "end": v(96.85, -50.26) * mm});
            skArc(sketch, "E951", {"start": v(96.85, -50.26) * mm, "mid": v(98.24, -49.58) * mm, "end": v(99.55, -48.76) * mm});
            skArc(sketch, "E952", {"start": v(99.55, -48.76) * mm, "mid": v(100.68, -47.87) * mm, "end": v(101.71, -46.87) * mm});
            skArc(sketch, "E953", {"start": v(101.71, -46.87) * mm, "mid": v(102.2, -46.08) * mm, "end": v(102.37, -45.18) * mm});
            skArc(sketch, "E954", {"start": v(102.37, -45.18) * mm, "mid": v(102.33, -44.67) * mm, "end": v(102.22, -44.17) * mm});
            skArc(sketch, "E955", {"start": v(102.22, -44.17) * mm, "mid": v(102.04, -43.93) * mm, "end": v(101.75, -43.84) * mm});
            skArc(sketch, "E956", {"start": v(101.75, -43.84) * mm, "mid": v(101.3, -43.91) * mm, "end": v(100.87, -44.1) * mm});
            skArc(sketch, "E957", {"start": v(100.87, -44.1) * mm, "mid": v(99.9, -44.69) * mm, "end": v(98.93, -45.3) * mm});
            skArc(sketch, "E958", {"start": v(98.93, -45.3) * mm, "mid": v(98.02, -45.81) * mm, "end": v(97.03, -46.19) * mm});
            skArc(sketch, "E959", {"start": v(97.03, -46.19) * mm, "mid": v(96.44, -46.17) * mm, "end": v(95.97, -45.8) * mm});
            skArc(sketch, "E960", {"start": v(95.97, -45.8) * mm, "mid": v(95.7, -45.12) * mm, "end": v(95.76, -44.4) * mm});
            skArc(sketch, "E961", {"start": v(95.76, -44.4) * mm, "mid": v(96.2, -43.17) * mm, "end": v(96.75, -42) * mm});
            skArc(sketch, "E962", {"start": v(96.75, -42) * mm, "mid": v(97.6, -40.17) * mm, "end": v(98.3, -38.28) * mm});
            skArc(sketch, "E963", {"start": v(98.3, -38.28) * mm, "mid": v(98.76, -36.54) * mm, "end": v(99.02, -34.76) * mm});
            skArc(sketch, "E964", {"start": v(99.02, -34.76) * mm, "mid": v(99.05, -33.27) * mm, "end": v(98.87, -31.8) * mm});
            skArc(sketch, "E965", {"start": v(98.87, -31.8) * mm, "mid": v(98.5, -30.68) * mm, "end": v(97.83, -29.7) * mm});
            skArc(sketch, "E966", {"start": v(97.83, -29.7) * mm, "mid": v(97.5, -29.31) * mm, "end": v(97.2, -28.9) * mm});
            skArc(sketch, "E967", {"start": v(97.2, -28.9) * mm, "mid": v(96.96, -28.52) * mm, "end": v(96.77, -28.12) * mm});
            skArc(sketch, "E968", {"start": v(96.77, -28.12) * mm, "mid": v(96.65, -27.8) * mm, "end": v(96.58, -27.47) * mm});
            skArc(sketch, "E969", {"start": v(96.58, -27.47) * mm, "mid": v(96.6, -27.26) * mm, "end": v(96.7, -27.08) * mm});
            skArc(sketch, "E970", {"start": v(96.7, -27.08) * mm, "mid": v(96.95, -26.62) * mm, "end": v(96.9, -26.1) * mm});
            skArc(sketch, "E971", {"start": v(96.9, -26.1) * mm, "mid": v(96.55, -25.48) * mm, "end": v(96.05, -24.97) * mm});
            skArc(sketch, "E972", {"start": v(96.05, -24.97) * mm, "mid": v(95.26, -24.45) * mm, "end": v(94.39, -24.07) * mm});
            skArc(sketch, "E973", {"start": v(94.39, -24.07) * mm, "mid": v(93.46, -23.84) * mm, "end": v(92.5, -23.77) * mm});
            skArc(sketch, "E974", {"start": v(92.5, -23.77) * mm, "mid": v(89.73, -24.12) * mm, "end": v(87.11, -25.09) * mm});
            skArc(sketch, "E975", {"start": v(87.11, -25.09) * mm, "mid": v(83.9, -26.94) * mm, "end": v(80.88, -29.1) * mm});
            skArc(sketch, "E976", {"start": v(80.88, -29.1) * mm, "mid": v(77.95, -31.69) * mm, "end": v(75.3, -34.55) * mm});
            skArc(sketch, "E977", {"start": v(75.3, -34.55) * mm, "mid": v(73.32, -37.3) * mm, "end": v(71.78, -40.31) * mm});
            skArc(sketch, "E978", {"start": v(71.78, -40.31) * mm, "mid": v(70.5, -42.66) * mm, "end": v(68.78, -44.7) * mm});
            skArc(sketch, "E979", {"start": v(68.78, -44.7) * mm, "mid": v(66.48, -46.6) * mm, "end": v(63.93, -48.14) * mm});
            skArc(sketch, "E980", {"start": v(63.93, -48.14) * mm, "mid": v(61.5, -49.12) * mm, "end": v(58.95, -49.69) * mm});
            skArc(sketch, "E981", {"start": v(58.95, -49.69) * mm, "mid": v(57.13, -49.51) * mm, "end": v(55.57, -48.55) * mm});
            skArc(sketch, "E982", {"start": v(55.57, -48.55) * mm, "mid": v(54.95, -47.7) * mm, "end": v(54.6, -46.7) * mm});
            skArc(sketch, "E983", {"start": v(54.6, -46.7) * mm, "mid": v(54.56, -45.62) * mm, "end": v(54.81, -44.56) * mm});
            skArc(sketch, "E984", {"start": v(54.81, -44.56) * mm, "mid": v(55.51, -43.12) * mm, "end": v(56.42, -41.8) * mm});
            skArc(sketch, "E985", {"start": v(56.42, -41.8) * mm, "mid": v(58.1, -39.75) * mm, "end": v(59.85, -37.78) * mm});
            skArc(sketch, "E986", {"start": v(59.85, -37.78) * mm, "mid": v(62.1, -35.2) * mm, "end": v(64.18, -32.48) * mm});
            skArc(sketch, "E987", {"start": v(64.18, -32.48) * mm, "mid": v(65.35, -30.51) * mm, "end": v(66.15, -28.37) * mm});
            skArc(sketch, "E988", {"start": v(66.15, -28.37) * mm, "mid": v(66.19, -27.06) * mm, "end": v(65.65, -25.87) * mm});
            skArc(sketch, "E989", {"start": v(65.65, -25.87) * mm, "mid": v(64.63, -25.04) * mm, "end": v(63.35, -24.75) * mm});
            skArc(sketch, "E990", {"start": v(63.35, -24.75) * mm, "mid": v(61.42, -25.1) * mm, "end": v(59.75, -26.13) * mm});
            skArc(sketch, "E991", {"start": v(59.75, -26.13) * mm, "mid": v(56.98, -28.78) * mm, "end": v(54.37, -31.6) * mm});
            skArc(sketch, "E992", {"start": v(54.37, -31.6) * mm, "mid": v(51.91, -34.58) * mm, "end": v(49.65, -37.72) * mm});
            skArc(sketch, "E993", {"start": v(49.65, -37.72) * mm, "mid": v(48.7, -39.7) * mm, "end": v(48.37, -41.87) * mm});
            skArc(sketch, "E994", {"start": v(48.37, -41.87) * mm, "mid": v(48.2, -42.83) * mm, "end": v(47.68, -43.66) * mm});
            skArc(sketch, "E995", {"start": v(47.68, -43.66) * mm, "mid": v(46.06, -45.36) * mm, "end": v(44.38, -47) * mm});
            skArc(sketch, "E996", {"start": v(44.38, -47) * mm, "mid": v(42.6, -48.6) * mm, "end": v(40.73, -50.11) * mm});
            skArc(sketch, "E997", {"start": v(40.73, -50.11) * mm, "mid": v(39.36, -51.02) * mm, "end": v(37.87, -51.73) * mm});
            skArc(sketch, "E998", {"start": v(37.87, -51.73) * mm, "mid": v(36.5, -51.93) * mm, "end": v(35.19, -51.5) * mm});
            skArc(sketch, "E999", {"start": v(35.19, -51.5) * mm, "mid": v(34.14, -50.51) * mm, "end": v(33.58, -49.19) * mm});
            skArc(sketch, "E1000", {"start": v(33.58, -49.19) * mm, "mid": v(33.36, -46.9) * mm, "end": v(33.6, -44.62) * mm});
            skArc(sketch, "E1001", {"start": v(33.6, -44.62) * mm, "mid": v(34.33, -41.61) * mm, "end": v(35.31, -38.67) * mm});
            skArc(sketch, "E1002", {"start": v(35.31, -38.67) * mm, "mid": v(35.88, -37.28) * mm, "end": v(36.52, -35.92) * mm});
            skArc(sketch, "E1003", {"start": v(36.52, -35.92) * mm, "mid": v(37.7, -33.63) * mm, "end": v(38.88, -31.35) * mm});
            skArc(sketch, "E1004", {"start": v(38.88, -31.35) * mm, "mid": v(40.3, -28.73) * mm, "end": v(41.74, -26.13) * mm});
            skArc(sketch, "E1005", {"start": v(41.74, -26.13) * mm, "mid": v(43.23, -23.51) * mm, "end": v(44.75, -20.91) * mm});
            skArc(sketch, "E1006", {"start": v(44.75, -20.91) * mm, "mid": v(47.5, -16.21) * mm, "end": v(50.2, -11.49) * mm});
            skArc(sketch, "E1007", {"start": v(50.2, -11.49) * mm, "mid": v(51.4, -9.13) * mm, "end": v(52.4, -6.68) * mm});
            skArc(sketch, "E1008", {"start": v(52.4, -6.68) * mm, "mid": v(52.78, -5.23) * mm, "end": v(52.84, -3.74) * mm});
            skArc(sketch, "E1009", {"start": v(52.84, -3.74) * mm, "mid": v(52.54, -2.61) * mm, "end": v(51.81, -1.7) * mm});
            skArc(sketch, "E1010", {"start": v(51.81, -1.7) * mm, "mid": v(51.32, -1.35) * mm, "end": v(50.78, -1.09) * mm});
            skArc(sketch, "E1011", {"start": v(50.78, -1.09) * mm, "mid": v(50.34, -1.01) * mm, "end": v(49.92, -1.1) * mm});
            skArc(sketch, "E1012", {"start": v(49.92, -1.1) * mm, "mid": v(49.39, -1.41) * mm, "end": v(48.93, -1.82) * mm});
            skArc(sketch, "E1013", {"start": v(48.93, -1.82) * mm, "mid": v(48.06, -2.78) * mm, "end": v(47.21, -3.77) * mm});
            skArc(sketch, "E1014", {"start": v(47.21, -3.77) * mm, "mid": v(46.46, -4.73) * mm, "end": v(45.77, -5.73) * mm});
            skArc(sketch, "E1015", {"start": v(45.77, -5.73) * mm, "mid": v(44.72, -7.39) * mm, "end": v(43.7, -9.07) * mm});
            skArc(sketch, "E1016", {"start": v(43.7, -9.07) * mm, "mid": v(42.56, -11) * mm, "end": v(41.46, -12.96) * mm});
            skArc(sketch, "E1017", {"start": v(41.46, -12.96) * mm, "mid": v(40.38, -14.93) * mm, "end": v(39.34, -16.91) * mm});
            skLineSegment(sketch, "E1018", {"start": v(39.34, -16.91) * mm, "end": v(34.38, -26.58) * mm});
            skLineSegment(sketch, "E1019", {"start": v(34.38, -26.58) * mm, "end": v(31.47, -25.48) * mm});
            skArc(sketch, "E1020", {"start": v(31.47, -25.48) * mm, "mid": v(30.57, -25.2) * mm, "end": v(29.64, -25.04) * mm});
            skArc(sketch, "E1021", {"start": v(29.64, -25.04) * mm, "mid": v(28.79, -25.02) * mm, "end": v(27.94, -25.13) * mm});
            skArc(sketch, "E1022", {"start": v(27.94, -25.13) * mm, "mid": v(26.83, -25.44) * mm, "end": v(25.77, -25.85) * mm});
            skArc(sketch, "E1023", {"start": v(25.77, -25.85) * mm, "mid": v(23.91, -26.7) * mm, "end": v(22.08, -27.57) * mm});
            skArc(sketch, "E1024", {"start": v(22.08, -27.57) * mm, "mid": v(19.43, -29) * mm, "end": v(16.9, -30.6) * mm});
            skArc(sketch, "E1025", {"start": v(16.9, -30.6) * mm, "mid": v(14.42, -32.43) * mm, "end": v(12.08, -34.41) * mm});
            skArc(sketch, "E1026", {"start": v(12.08, -34.41) * mm, "mid": v(10.14, -36.3) * mm, "end": v(8.34, -38.3) * mm});
            skArc(sketch, "E1027", {"start": v(8.34, -38.3) * mm, "mid": v(7.35, -39.8) * mm, "end": v(6.72, -41.49) * mm});
            skArc(sketch, "E1028", {"start": v(6.72, -41.49) * mm, "mid": v(6.2, -42.77) * mm, "end": v(5.32, -43.85) * mm});
            skArc(sketch, "E1029", {"start": v(5.32, -43.85) * mm, "mid": v(3.6, -45.32) * mm, "end": v(1.78, -46.67) * mm});
            skArc(sketch, "E1030", {"start": v(1.78, -46.67) * mm, "mid": v(-0.1, -47.87) * mm, "end": v(-2.07, -48.93) * mm});
            skArc(sketch, "E1031", {"start": v(-2.07, -48.93) * mm, "mid": v(-3.18, -49.22) * mm, "end": v(-4.31, -49.04) * mm});
            skArc(sketch, "E1032", {"start": v(-4.31, -49.04) * mm, "mid": v(-5.04, -48.48) * mm, "end": v(-5.35, -47.61) * mm});
            skArc(sketch, "E1033", {"start": v(-5.35, -47.61) * mm, "mid": v(-5.29, -46.23) * mm, "end": v(-4.97, -44.88) * mm});
            skArc(sketch, "E1034", {"start": v(-4.97, -44.88) * mm, "mid": v(-4.15, -42.8) * mm, "end": v(-3.12, -40.82) * mm});
            skArc(sketch, "E1035", {"start": v(-3.12, -40.82) * mm, "mid": v(-1.43, -38.02) * mm, "end": v(0.35, -35.28) * mm});
            skArc(sketch, "E1036", {"start": v(0.35, -35.28) * mm, "mid": v(1.47, -33.58) * mm, "end": v(2.54, -31.86) * mm});
            skArc(sketch, "E1037", {"start": v(2.54, -31.86) * mm, "mid": v(3.35, -30.42) * mm, "end": v(4.1, -28.95) * mm});
            skArc(sketch, "E1038", {"start": v(4.1, -28.95) * mm, "mid": v(4.62, -27.77) * mm, "end": v(5.08, -26.56) * mm});
            skArc(sketch, "E1039", {"start": v(5.08, -26.56) * mm, "mid": v(5.3, -25.7) * mm, "end": v(5.37, -24.8) * mm});
            skArc(sketch, "E1040", {"start": v(5.37, -24.8) * mm, "mid": v(5.16, -23.53) * mm, "end": v(4.54, -22.42) * mm});
            skArc(sketch, "E1041", {"start": v(4.54, -22.42) * mm, "mid": v(3.7, -21.9) * mm, "end": v(2.73, -22) * mm});
            skArc(sketch, "E1042", {"start": v(2.73, -22) * mm, "mid": v(1.03, -23.01) * mm, "end": v(-0.44, -24.33) * mm});
            skArc(sketch, "E1043", {"start": v(-0.44, -24.33) * mm, "mid": v(-2.85, -27.01) * mm, "end": v(-5.15, -29.79) * mm});
            skArc(sketch, "E1044", {"start": v(-5.15, -29.79) * mm, "mid": v(-7.59, -32.67) * mm, "end": v(-10.17, -35.43) * mm});
            skArc(sketch, "E1045", {"start": v(-10.17, -35.43) * mm, "mid": v(-13.34, -38.53) * mm, "end": v(-16.61, -41.54) * mm});
            skArc(sketch, "E1046", {"start": v(-16.61, -41.54) * mm, "mid": v(-19.81, -44.34) * mm, "end": v(-23.06, -47.1) * mm});
            skArc(sketch, "E1047", {"start": v(-23.06, -47.1) * mm, "mid": v(-23.98, -47.52) * mm, "end": v(-24.99, -47.43) * mm});
            skArc(sketch, "E1048", {"start": v(-24.99, -47.43) * mm, "mid": v(-25.67, -46.92) * mm, "end": v(-25.92, -46.1) * mm});
            skArc(sketch, "E1049", {"start": v(-25.92, -46.1) * mm, "mid": v(-25.78, -44.85) * mm, "end": v(-25.37, -43.66) * mm});
            skArc(sketch, "E1050", {"start": v(-25.37, -43.66) * mm, "mid": v(-24.4, -41.9) * mm, "end": v(-23.25, -40.26) * mm});
            skArc(sketch, "E1051", {"start": v(-23.25, -40.26) * mm, "mid": v(-21.53, -38.2) * mm, "end": v(-19.7, -36.25) * mm});
            skArc(sketch, "E1052", {"start": v(-19.7, -36.25) * mm, "mid": v(-17.43, -33.86) * mm, "end": v(-15.2, -31.43) * mm});
            skArc(sketch, "E1053", {"start": v(-15.2, -31.43) * mm, "mid": v(-14, -29.97) * mm, "end": v(-12.97, -28.4) * mm});
            skArc(sketch, "E1054", {"start": v(-12.97, -28.4) * mm, "mid": v(-12.58, -27.49) * mm, "end": v(-12.44, -26.5) * mm});
            skArc(sketch, "E1055", {"start": v(-12.44, -26.5) * mm, "mid": v(-12.65, -25.8) * mm, "end": v(-13.23, -25.35) * mm});
            skArc(sketch, "E1056", {"start": v(-13.23, -25.35) * mm, "mid": v(-14.4, -24.99) * mm, "end": v(-15.62, -24.8) * mm});
            skArc(sketch, "E1057", {"start": v(-15.62, -24.8) * mm, "mid": v(-16.75, -24.8) * mm, "end": v(-17.87, -25) * mm});
            skArc(sketch, "E1058", {"start": v(-17.87, -25) * mm, "mid": v(-18.99, -25.4) * mm, "end": v(-20.02, -25.98) * mm});
            skArc(sketch, "E1059", {"start": v(-20.02, -25.98) * mm, "mid": v(-21.12, -26.8) * mm, "end": v(-22.13, -27.75) * mm});
            skArc(sketch, "E1060", {"start": v(-22.13, -27.75) * mm, "mid": v(-23.2, -28.78) * mm, "end": v(-24.37, -29.71) * mm});
            skArc(sketch, "E1061", {"start": v(-24.37, -29.71) * mm, "mid": v(-25.32, -30.26) * mm, "end": v(-26.37, -30.6) * mm});
            skArc(sketch, "E1062", {"start": v(-26.37, -30.6) * mm, "mid": v(-27.3, -30.64) * mm, "end": v(-28.2, -30.44) * mm});
            skArc(sketch, "E1063", {"start": v(-28.2, -30.44) * mm, "mid": v(-29.11, -29.97) * mm, "end": v(-29.91, -29.32) * mm});
            skArc(sketch, "E1064", {"start": v(-29.91, -29.32) * mm, "mid": v(-30.29, -29) * mm, "end": v(-30.71, -28.74) * mm});
            skArc(sketch, "E1065", {"start": v(-30.71, -28.74) * mm, "mid": v(-31.34, -28.46) * mm, "end": v(-31.98, -28.21) * mm});
            skArc(sketch, "E1066", {"start": v(-31.98, -28.21) * mm, "mid": v(-32.7, -27.98) * mm, "end": v(-33.45, -27.8) * mm});
            skArc(sketch, "E1067", {"start": v(-33.45, -27.8) * mm, "mid": v(-34.18, -27.66) * mm, "end": v(-34.92, -27.57) * mm});
            skLineSegment(sketch, "E1068", {"start": v(-34.92, -27.57) * mm, "end": v(-38.5, -27.25) * mm});
            skLineSegment(sketch, "E1069", {"start": v(-38.5, -27.25) * mm, "end": v(-31.07, -14.25) * mm});
            skArc(sketch, "E1070", {"start": v(-31.07, -14.25) * mm, "mid": v(-28.71, -10.08) * mm, "end": v(-26.4, -5.9) * mm});
            skArc(sketch, "E1071", {"start": v(-26.4, -5.9) * mm, "mid": v(-25.36, -3.82) * mm, "end": v(-24.46, -1.7) * mm});
            skArc(sketch, "E1072", {"start": v(-24.46, -1.7) * mm, "mid": v(-24.04, -0.3) * mm, "end": v(-23.84, 1.14) * mm});
            skArc(sketch, "E1073", {"start": v(-23.84, 1.14) * mm, "mid": v(-23.9, 2.42) * mm, "end": v(-24.23, 3.67) * mm});
            skArc(sketch, "E1074", {"start": v(-24.23, 3.67) * mm, "mid": v(-24.54, 4.24) * mm, "end": v(-24.97, 4.72) * mm});
            skArc(sketch, "E1075", {"start": v(-24.97, 4.72) * mm, "mid": v(-25.42, 4.94) * mm, "end": v(-25.92, 4.92) * mm});
            skArc(sketch, "E1076", {"start": v(-25.92, 4.92) * mm, "mid": v(-26.8, 4.6) * mm, "end": v(-27.62, 4.17) * mm});
            skArc(sketch, "E1077", {"start": v(-27.62, 4.17) * mm, "mid": v(-30.13, 2.65) * mm, "end": v(-32.63, 1.12) * mm});
            skLineSegment(sketch, "E1078", {"start": v(-39.66, -15.67) * mm, "end": v(-46.88, -27.75) * mm});
            skLineSegment(sketch, "E1079", {"start": v(-46.88, -27.75) * mm, "end": v(-54.5, -27.72) * mm});
            skLineSegment(sketch, "E1080", {"start": v(-54.5, -27.72) * mm, "end": v(-62.13, -27.69) * mm});
            skLineSegment(sketch, "E1081", {"start": v(-62.13, -27.69) * mm, "end": v(-54.63, -20.44) * mm});
            skArc(sketch, "E1082", {"start": v(-54.63, -20.44) * mm, "mid": v(-51.51, -17.51) * mm, "end": v(-48.32, -14.67) * mm});
            skArc(sketch, "E1083", {"start": v(-48.32, -14.67) * mm, "mid": v(-44.74, -11.64) * mm, "end": v(-41.1, -8.7) * mm});
            skArc(sketch, "E1084", {"start": v(-41.1, -8.7) * mm, "mid": v(-37.54, -5.88) * mm, "end": v(-33.96, -3.1) * mm});
            skArc(sketch, "E1085", {"start": v(-33.96, -3.1) * mm, "mid": v(-33.4, -2.93) * mm, "end": v(-32.87, -3.17) * mm});
            skArc(sketch, "E1086", {"start": v(-32.87, -3.17) * mm, "mid": v(-32.79, -3.34) * mm, "end": v(-32.82, -3.54) * mm});
            skArc(sketch, "E1087", {"start": v(-32.82, -3.54) * mm, "mid": v(-33.75, -5.28) * mm, "end": v(-34.7, -7.02) * mm});
            skArc(sketch, "E1088", {"start": v(-34.7, -7.02) * mm, "mid": v(-35.8, -9.02) * mm, "end": v(-36.93, -11.01) * mm});
            skArc(sketch, "E1089", {"start": v(-36.93, -11.01) * mm, "mid": v(-38.28, -13.35) * mm, "end": v(-39.66, -15.67) * mm});
            skArc(sketch, "E1090", {"start": v(89.7, -36.34) * mm, "mid": v(89.12, -37.68) * mm, "end": v(88.58, -39.05) * mm});
            skArc(sketch, "E1091", {"start": v(88.58, -39.05) * mm, "mid": v(88.2, -40.2) * mm, "end": v(87.89, -41.37) * mm});
            skArc(sketch, "E1092", {"start": v(87.89, -41.37) * mm, "mid": v(87.7, -42.37) * mm, "end": v(87.59, -43.39) * mm});
            skArc(sketch, "E1093", {"start": v(87.59, -43.39) * mm, "mid": v(87.58, -44.29) * mm, "end": v(87.67, -45.18) * mm});
            skArc(sketch, "E1094", {"start": v(87.67, -45.18) * mm, "mid": v(87.78, -46.08) * mm, "end": v(87.84, -46.98) * mm});
            skArc(sketch, "E1095", {"start": v(87.84, -46.98) * mm, "mid": v(87.78, -47.58) * mm, "end": v(87.6, -48.14) * mm});
            skArc(sketch, "E1096", {"start": v(87.6, -48.14) * mm, "mid": v(87.28, -48.64) * mm, "end": v(86.87, -49.06) * mm});
            skArc(sketch, "E1097", {"start": v(86.87, -49.06) * mm, "mid": v(86.14, -49.6) * mm, "end": v(85.38, -50.09) * mm});
            skArc(sketch, "E1098", {"start": v(85.38, -50.09) * mm, "mid": v(84.2, -50.72) * mm, "end": v(82.95, -51.24) * mm});
            skArc(sketch, "E1099", {"start": v(82.95, -51.24) * mm, "mid": v(81.86, -51.54) * mm, "end": v(80.74, -51.68) * mm});
            skArc(sketch, "E1100", {"start": v(80.74, -51.68) * mm, "mid": v(79.8, -51.63) * mm, "end": v(78.9, -51.4) * mm});
            skArc(sketch, "E1101", {"start": v(78.9, -51.4) * mm, "mid": v(78.15, -51) * mm, "end": v(77.53, -50.43) * mm});
            skArc(sketch, "E1102", {"start": v(77.53, -50.43) * mm, "mid": v(77.06, -49.58) * mm, "end": v(76.94, -48.62) * mm});
            skArc(sketch, "E1103", {"start": v(76.94, -48.62) * mm, "mid": v(77.13, -46.96) * mm, "end": v(77.45, -45.33) * mm});
            skArc(sketch, "E1104", {"start": v(77.45, -45.33) * mm, "mid": v(77.96, -43.58) * mm, "end": v(78.62, -41.9) * mm});
            skArc(sketch, "E1105", {"start": v(78.62, -41.9) * mm, "mid": v(79.32, -40.56) * mm, "end": v(80.22, -39.35) * mm});
            skArc(sketch, "E1106", {"start": v(80.22, -39.35) * mm, "mid": v(80.99, -38.56) * mm, "end": v(81.83, -37.86) * mm});
            skArc(sketch, "E1107", {"start": v(81.83, -37.86) * mm, "mid": v(84, -36.24) * mm, "end": v(86.18, -34.65) * mm});
            skArc(sketch, "E1108", {"start": v(86.18, -34.65) * mm, "mid": v(88.44, -33.03) * mm, "end": v(90.71, -31.43) * mm});
            skArc(sketch, "E1109", {"start": v(90.71, -31.43) * mm, "mid": v(91.36, -31.05) * mm, "end": v(92.07, -30.8) * mm});
            skArc(sketch, "E1110", {"start": v(92.07, -30.8) * mm, "mid": v(92.1, -30.81) * mm, "end": v(92.11, -30.85) * mm});
            skArc(sketch, "E1111", {"start": v(92.11, -30.85) * mm, "mid": v(91.79, -31.63) * mm, "end": v(91.45, -32.4) * mm});
            skArc(sketch, "E1112", {"start": v(91.45, -32.4) * mm, "mid": v(91.07, -33.3) * mm, "end": v(90.67, -34.2) * mm});
            skArc(sketch, "E1113", {"start": v(90.67, -34.2) * mm, "mid": v(90.19, -35.27) * mm, "end": v(89.7, -36.34) * mm});
            skArc(sketch, "E1114", {"start": v(31.67, -33.73) * mm, "mid": v(31, -35.37) * mm, "end": v(29.94, -36.78) * mm});
            skArc(sketch, "E1115", {"start": v(29.94, -36.78) * mm, "mid": v(26.6, -40.1) * mm, "end": v(23.19, -43.36) * mm});
            skArc(sketch, "E1116", {"start": v(23.19, -43.36) * mm, "mid": v(19.67, -46.6) * mm, "end": v(16.1, -49.77) * mm});
            skArc(sketch, "E1117", {"start": v(16.1, -49.77) * mm, "mid": v(14.88, -50.5) * mm, "end": v(13.48, -50.75) * mm});
            skArc(sketch, "E1118", {"start": v(13.48, -50.75) * mm, "mid": v(12.95, -50.56) * mm, "end": v(12.65, -50.08) * mm});
            skArc(sketch, "E1119", {"start": v(12.65, -50.08) * mm, "mid": v(12.47, -49) * mm, "end": v(12.43, -47.92) * mm});
            skArc(sketch, "E1120", {"start": v(12.43, -47.92) * mm, "mid": v(12.53, -46.56) * mm, "end": v(12.76, -45.22) * mm});
            skArc(sketch, "E1121", {"start": v(12.76, -45.22) * mm, "mid": v(13.13, -43.99) * mm, "end": v(13.64, -42.8) * mm});
            skArc(sketch, "E1122", {"start": v(13.64, -42.8) * mm, "mid": v(14.4, -41.7) * mm, "end": v(15.41, -40.81) * mm});
            skArc(sketch, "E1123", {"start": v(15.41, -40.81) * mm, "mid": v(18.73, -38.65) * mm, "end": v(22.08, -36.55) * mm});
            skArc(sketch, "E1124", {"start": v(22.08, -36.55) * mm, "mid": v(25.46, -34.5) * mm, "end": v(28.87, -32.51) * mm});
            skArc(sketch, "E1125", {"start": v(28.87, -32.51) * mm, "mid": v(30.16, -31.98) * mm, "end": v(31.53, -31.77) * mm});
            skArc(sketch, "E1126", {"start": v(31.53, -31.77) * mm, "mid": v(31.66, -31.8) * mm, "end": v(31.74, -31.9) * mm});
            skArc(sketch, "E1127", {"start": v(31.74, -31.9) * mm, "mid": v(31.8, -32.12) * mm, "end": v(31.84, -32.34) * mm});
            skArc(sketch, "E1128", {"start": v(31.84, -32.34) * mm, "mid": v(31.85, -32.65) * mm, "end": v(31.82, -32.97) * mm});
            skArc(sketch, "E1129", {"start": v(31.82, -32.97) * mm, "mid": v(31.76, -33.35) * mm, "end": v(31.67, -33.73) * mm});
            skArc(sketch, "E1130", {"start": v(67.7, -13) * mm, "mid": v(66.5, -14.51) * mm, "end": v(65.5, -16.17) * mm});
            skArc(sketch, "E1131", {"start": v(65.5, -16.17) * mm, "mid": v(65.02, -17.56) * mm, "end": v(64.93, -19.03) * mm});
            skArc(sketch, "E1132", {"start": v(64.93, -19.03) * mm, "mid": v(65.27, -20.12) * mm, "end": v(66.03, -20.97) * mm});
            skArc(sketch, "E1133", {"start": v(66.03, -20.97) * mm, "mid": v(67.16, -21.55) * mm, "end": v(68.42, -21.75) * mm});
            skArc(sketch, "E1134", {"start": v(68.42, -21.75) * mm, "mid": v(69.95, -21.43) * mm, "end": v(71.23, -20.54) * mm});
            skArc(sketch, "E1135", {"start": v(71.23, -20.54) * mm, "mid": v(72.52, -18.9) * mm, "end": v(73.5, -17.06) * mm});
            skArc(sketch, "E1136", {"start": v(73.5, -17.06) * mm, "mid": v(74.04, -15.26) * mm, "end": v(74.2, -13.37) * mm});
            skArc(sketch, "E1137", {"start": v(74.2, -13.37) * mm, "mid": v(73.8, -12.15) * mm, "end": v(72.8, -11.36) * mm});
            skArc(sketch, "E1138", {"start": v(72.8, -11.36) * mm, "mid": v(72, -11.08) * mm, "end": v(71.2, -10.87) * mm});
            skArc(sketch, "E1139", {"start": v(71.2, -10.87) * mm, "mid": v(70.67, -10.83) * mm, "end": v(70.15, -10.92) * mm});
            skArc(sketch, "E1140", {"start": v(70.15, -10.92) * mm, "mid": v(69.62, -11.16) * mm, "end": v(69.16, -11.5) * mm});
            skArc(sketch, "E1141", {"start": v(69.16, -11.5) * mm, "mid": v(68.42, -12.23) * mm, "end": v(67.7, -13) * mm});
            skSolve(sketch);
        }
        {
            var Q0;
            Q0=makeQuery(id+"F0.imprint","IMPRINT",FACE,{"disambiguationData":[TD([[makeQuery(id+"F0.imprint","IMPRINT",EDGE,{"derivedFrom":sQuery(id+"F0.wireOp",EDGE,"E0")}),1.0]])]});
            var Q1;
            Q1=makeQuery(id+"F0.imprint","IMPRINT",FACE,{"disambiguationData":[TD([[makeQuery(id+"F0.imprint","IMPRINT",EDGE,{"derivedFrom":sQuery(id+"F0.wireOp",EDGE,"E798")}),1.0]])]});
            extrude(context, id + "F1", {"entities" : qUnion([Q0, Q1]), "depth" : 6 * mm, "offsetDistance" : 25 * mm});
        }
    });
